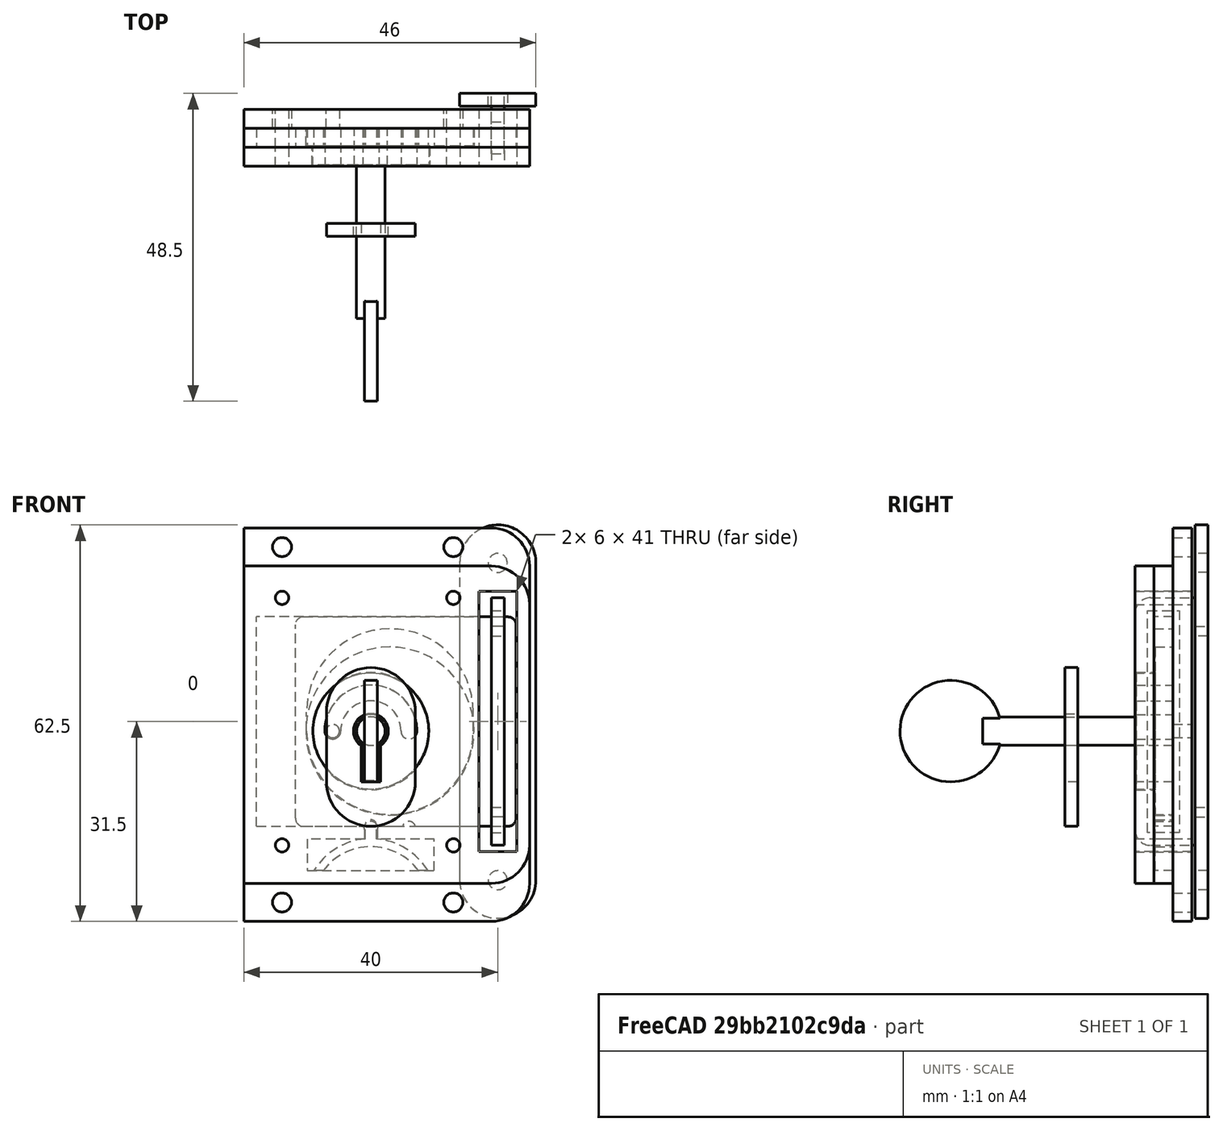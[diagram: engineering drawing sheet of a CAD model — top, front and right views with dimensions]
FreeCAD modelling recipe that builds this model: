
FCSTD DOCUMENT  (FreeCAD 0.21R33492 (Git))
Label: DoorLock
License: All rights reserved
LicenseURL: http://en.wikipedia.org/wiki/All_rights_reserved
objects: TechDraw::DrawViewDimension×39, Sketcher::SketchObject×13, Part::Extrusion×10, TechDraw::DrawViewPart×6, TechDraw::DrawHatch×3, Part::MultiFuse×2, TechDraw::DrawSVGTemplate×2, App::DocumentObjectGroup×2, Part::Cylinder×2, TechDraw::DrawPage×2, Part::Box×1
note: 28 computed .brp shape members not serialized (recipe doc carries the construction recipe); baked Part::Feature solids carry a one-line shape summary decoded from their .brp

FEATURE [Sketcher::SketchObject] Sketch  label="TopPartShape"
  FullyConstrained = true
  Placement = pos=(0,0,0) rot=(1,0,0;1.5708rad)
  sketch-geometry (9):
    g0: ArcOfCircle CenterX=0 CenterY=0 CenterZ=0 NormalX=0 NormalY=0 NormalZ=1 AngleXU=0 Radius=2.625 StartAngle=5.20871 EndAngle=10.4993
    g1: LineSegment StartX=-1.25 StartY=-2.30827 StartZ=0 EndX=-1.25 EndY=-8 EndZ=0
    g2: LineSegment StartX=-1.25 StartY=-8 StartZ=0 EndX=1.25 EndY=-8 EndZ=0
    g3: LineSegment StartX=1.25 StartY=-8 StartZ=0 EndX=1.25 EndY=-2.30827 EndZ=0
    g4: Circle CenterX=0 CenterY=0 CenterZ=0 NormalX=0 NormalY=0 NormalZ=1 AngleXU=0 Radius=9.25
    g5: ArcOfCircle CenterX=-6 CenterY=0 CenterZ=0 NormalX=0 NormalY=0 NormalZ=1 AngleXU=0 Radius=1.25 StartAngle=3.14159 EndAngle=6.28319
    g6: ArcOfCircle CenterX=6 CenterY=0 CenterZ=0 NormalX=0 NormalY=0 NormalZ=1 AngleXU=0 Radius=1.25 StartAngle=3.14159 EndAngle=6.28319
    g7: ArcOfCircle CenterX=0 CenterY=0 CenterZ=0 NormalX=0 NormalY=0 NormalZ=1 AngleXU=0 Radius=7.25 StartAngle=0 EndAngle=3.14159
    g8: ArcOfCircle CenterX=0 CenterY=0 CenterZ=0 NormalX=0 NormalY=0 NormalZ=1 AngleXU=0 Radius=4.75 StartAngle=0 EndAngle=3.14159
  constraints (28):
    c: Coincident(g0,g-1)
    c: Coincident(g1,g0)
    c: Vertical(g1)
    c: Coincident(g2,g1)
    c: Horizontal(g2)
    c: Coincident(g3,g2)
    c: Coincident(g3,g0)
    c: Vertical(g3)
    c: Diameter(g0) = 5.25
    c: Distance(g2) = 2.5
    c: Horizontal(g0,g0)
    c: DistanceY(g2,g0) = 8
    c: Coincident(g4,g0)
    c: Diameter(g4) = 18.5
    c: PointOnObject(g5,g-1)
    c: PointOnObject(g5,g-1)
    c: PointOnObject(g5,g-1)
    c: PointOnObject(g6,g-1)
    c: PointOnObject(g6,g-1)
    c: PointOnObject(g6,g-1)
    c: Coincident(g7,g0)
    c: Coincident(g7,g5)
    c: Coincident(g7,g6)
    c: Coincident(g8,g0)
    c: Coincident(g8,g5)
    c: Coincident(g8,g6)
    c: Diameter(g5) = 2.5
    c: DistanceX(g5,g6) = 12
FEATURE [Sketcher::SketchObject] Sketch001  label="BottomPartShape"
  FullyConstrained = true
  Placement = pos=(0,0,0) rot=(1,0,0;1.5708rad)
  expr: Constraints[20] = Sketch.Constraints[8]
  expr: Constraints[21] = Sketch.Constraints[9]
  expr: Constraints[23] = Sketch.Constraints[11]
  expr: Constraints[36] = Sketch.Constraints[26]
  expr: Constraints[37] = Sketch.Constraints[27]
  sketch-geometry (13):
    g0: Circle CenterX=0 CenterY=0 CenterZ=0 NormalX=0 NormalY=0 NormalZ=1 AngleXU=0 Radius=10.25
    g1: GeomPoint X=-10.25 Y=0 Z=0
    g2: Circle CenterX=3 CenterY=0 CenterZ=0 NormalX=0 NormalY=0 NormalZ=1 AngleXU=0 Radius=13.25
    g3: GeomPoint X=16.25 Y=0 Z=0
    g4: GeomPoint X=10.25 Y=0 Z=0
    g5: ArcOfCircle CenterX=0 CenterY=0 CenterZ=0 NormalX=0 NormalY=0 NormalZ=1 AngleXU=0 Radius=2.625 StartAngle=5.20871 EndAngle=10.4993
    g6: LineSegment StartX=-1.25 StartY=-2.30827 StartZ=0 EndX=-1.25 EndY=-8 EndZ=0
    g7: LineSegment StartX=-1.25 StartY=-8 StartZ=0 EndX=1.25 EndY=-8 EndZ=0
    g8: LineSegment StartX=1.25 StartY=-8 StartZ=0 EndX=1.25 EndY=-2.30827 EndZ=0
    g9: ArcOfCircle CenterX=-6 CenterY=0 CenterZ=0 NormalX=0 NormalY=0 NormalZ=1 AngleXU=0 Radius=1.25 StartAngle=3.14159 EndAngle=6.28319
    g10: ArcOfCircle CenterX=6 CenterY=0 CenterZ=0 NormalX=0 NormalY=0 NormalZ=1 AngleXU=0 Radius=1.25 StartAngle=3.14159 EndAngle=6.28319
    g11: ArcOfCircle CenterX=0 CenterY=0 CenterZ=0 NormalX=0 NormalY=0 NormalZ=1 AngleXU=0 Radius=7.25 StartAngle=0 EndAngle=3.14159
    g12: ArcOfCircle CenterX=0 CenterY=0 CenterZ=0 NormalX=0 NormalY=0 NormalZ=1 AngleXU=0 Radius=4.75 StartAngle=0 EndAngle=3.14159
  constraints (38):
    c: Diameter(g0) = 20.5
    c: PointOnObject(g1,g-1)
    c: PointOnObject(g1,g0)
    c: PointOnObject(g2,g-1)
    c: PointOnObject(g1,g2)
    c: Diameter(g2) = 26.5
    c: PointOnObject(g3,g-1)
    c: PointOnObject(g3,g2)
    c: PointOnObject(g4,g0)
    c: PointOnObject(g4,g-1)
    c: DistanceX(g4,g3) = 6
    c: Coincident(g0,g-1)
    c: Coincident(g5,g-1)
    c: Coincident(g6,g5)
    c: Vertical(g6)
    c: Coincident(g7,g6)
    c: Horizontal(g7)
    c: Coincident(g8,g7)
    c: Coincident(g8,g5)
    c: Vertical(g8)
    c: Diameter(g5) = 5.25
    c: Distance(g7) = 2.5
    c: Horizontal(g5,g5)
    c: DistanceY(g7,g5) = 8
    c: PointOnObject(g9,g-1)
    c: PointOnObject(g9,g-1)
    c: PointOnObject(g9,g-1)
    c: PointOnObject(g10,g-1)
    c: PointOnObject(g10,g-1)
    c: PointOnObject(g10,g-1)
    c: Coincident(g11,g5)
    c: Coincident(g11,g9)
    c: Coincident(g11,g10)
    c: Coincident(g12,g5)
    c: Coincident(g12,g9)
    c: Coincident(g12,g10)
    c: Diameter(g9) = 2.5
    c: DistanceX(g9,g10) = 12
FEATURE [Sketcher::SketchObject] Sketch002  label="SliderShape"
  FullyConstrained = true
  Placement = pos=(0,0,0) rot=(1,0,0;1.5708rad)
  sketch-geometry (25):
    g0: LineSegment StartX=-10.625 StartY=18 StartZ=0 EndX=21.625 EndY=18 EndZ=0
    g1: LineSegment StartX=21.625 StartY=-15 StartZ=0 EndX=-10.625 EndY=-15 EndZ=0
    g2: LineSegment StartX=-11.875 StartY=-13.75 StartZ=0 EndX=-11.875 EndY=16.75 EndZ=0
    g3: LineSegment StartX=22.875 StartY=16.75 StartZ=0 EndX=22.875 EndY=-13.75 EndZ=0
    g4: ArcOfCircle CenterX=3 CenterY=3 CenterZ=0 NormalX=0 NormalY=0 NormalZ=1 AngleXU=0 Radius=13.125 StartAngle=0 EndAngle=3.14159
    g5: ArcOfCircle CenterX=3 CenterY=0 CenterZ=0 NormalX=0 NormalY=0 NormalZ=1 AngleXU=0 Radius=13.125 StartAngle=3.14159 EndAngle=6.28319
    g6: LineSegment StartX=-10.125 StartY=1.6e-15 StartZ=0 EndX=-10.125 EndY=3 EndZ=0
    g7: LineSegment StartX=16.125 StartY=1.6e-15 StartZ=0 EndX=16.125 EndY=3 EndZ=0
    g8: LineSegment StartX=-10.125 StartY=3 StartZ=0 EndX=16.125 EndY=3 EndZ=0
    g9: LineSegment StartX=16.125 StartY=1.6e-15 StartZ=0 EndX=-10.125 EndY=1.6e-15 EndZ=0
    g10: ArcOfCircle CenterX=-10.625 CenterY=16.75 CenterZ=0 NormalX=0 NormalY=0 NormalZ=1 AngleXU=0 Radius=1.25 StartAngle=1.5708 EndAngle=3.14159
    g11: GeomPoint X=-11.875 Y=18 Z=0
    g12: ArcOfCircle CenterX=-10.625 CenterY=-13.75 CenterZ=0 NormalX=0 NormalY=0 NormalZ=1 AngleXU=0 Radius=1.25 StartAngle=3.14159 EndAngle=4.71239
    g13: GeomPoint X=-11.875 Y=-15 Z=0
    g14: ArcOfCircle CenterX=21.625 CenterY=16.75 CenterZ=0 NormalX=0 NormalY=0 NormalZ=1 AngleXU=0 Radius=1.25 StartAngle=-9e-16 EndAngle=1.5708
    g15: GeomPoint X=22.875 Y=18 Z=0
    g16: ArcOfCircle CenterX=21.625 CenterY=-13.75 CenterZ=0 NormalX=0 NormalY=0 NormalZ=1 AngleXU=0 Radius=1.25 StartAngle=4.71239 EndAngle=6.28319
    g17: GeomPoint X=22.875 Y=-15 Z=0
    g18: LineSegment StartX=-10.625 StartY=-15 StartZ=0 EndX=-1 EndY=-15 EndZ=0
    g19: LineSegment StartX=7 StartY=-15 StartZ=0 EndX=21.625 EndY=-15 EndZ=0
    g20: ArcOfCircle CenterX=-2e-16 CenterY=-15.25 CenterZ=0 NormalX=0 NormalY=0 NormalZ=1 AngleXU=0 Radius=1.03078 StartAngle=0.244979 EndAngle=2.89661
    g21: ArcOfCircle CenterX=6 CenterY=-15.25 CenterZ=0 NormalX=0 NormalY=0 NormalZ=1 AngleXU=0 Radius=1.03078 StartAngle=0.244979 EndAngle=2.89661
    g22: LineSegment StartX=1 StartY=-15 StartZ=0 EndX=3 EndY=-15 EndZ=0
    g23: LineSegment StartX=3 StartY=-15 StartZ=0 EndX=5 EndY=-15 EndZ=0
    g24: LineSegment StartX=-2e-16 StartY=-15.25 StartZ=0 EndX=6 EndY=-15.25 EndZ=0
  constraints (68):
    c: Horizontal(g0)
    c: Horizontal(g1)
    c: Vertical(g2)
    c: Vertical(g3)
    c: Coincident(g6,g5)
    c: Coincident(g6,g4)
    c: Coincident(g7,g5)
    c: Coincident(g7,g4)
    c: Vertical(g6)
    c: Vertical(g7)
    c: DistanceY(g5,g4) = 3
    c: Coincident(g8,g4)
    c: Coincident(g8,g4)
    c: Horizontal(g8)
    c: Coincident(g9,g5)
    c: Coincident(g9,g5)
    c: Horizontal(g9)
    c: PointOnObject(g4,g8)
    c: PointOnObject(g5,g9)
    c: Diameter(g4) = 26.25
    c: PointOnObject(g5,g-1)
    c: DistanceX(g-1,g5) = 3
    c: DistanceX(g11,g-1) = 11.875
    c: Distance(g15,g11) = 34.75
    c: DistanceY(g-1,g11) = 18
    c: PointOnObject(g11,g2)
    c: PointOnObject(g11,g0)
    c: Tangent(g2,g10) = 1.5708
    c: Tangent(g0,g10) = 1.5708
    c: PointOnObject(g13,g2)
    c: PointOnObject(g13,g1)
    c: Tangent(g2,g12) = 1.5708
    c: Tangent(g1,g12) = 1.5708
    c: Equal(g10,g12)
    c: Diameter(g10) = 2.5
    c: PointOnObject(g15,g0)
    c: PointOnObject(g15,g3)
    c: Tangent(g0,g14) = 1.5708
    c: Tangent(g3,g14) = 1.5708
    c: PointOnObject(g17,g1)
    c: PointOnObject(g17,g3)
    c: Tangent(g1,g16) = 1.5708
    c: Tangent(g3,g16) = 1.5708
    c: Equal(g10,g14)
    c: Equal(g10,g16)
    c: Coincident(g18,g12)
    c: PointOnObject(g18,g1)
    c: PointOnObject(g22,g1)
    c: PointOnObject(g23,g1)
    c: PointOnObject(g19,g1)
    c: Coincident(g19,g16)
    c: Coincident(g20,g18)
    c: Coincident(g20,g22)
    c: Coincident(g21,g23)
    c: Coincident(g21,g19)
    c: Equal(g20,g21)
    c: DistanceX(g20,g21) = 6
    c: Coincident(g22,g23)
    c: Equal(g22,g23)
    c: DistanceX(g-1,g22) = 3
    c: PointOnObject(g22,g1)
    c: Coincident(g24,g20)
    c: Coincident(g24,g21)
    c: Horizontal(g24)
    c: DistanceY(g20,g18) = 0.25
    c: DistanceX(g18,g20) = 2
    c: DistanceY(g13,g-1) = 15
    c: DistanceY(g13,g11) = 33
FEATURE [Sketcher::SketchObject] Sketch003  label="SpacerShape"
  FullyConstrained = true
  Placement = pos=(0,0,0) rot=(1,0,0;1.5708rad)
  expr: Constraints[38] = Sketch021.Constraints[8]
  expr: Constraints[39] = Sketch021.Constraints[9]
  expr: Constraints[40] = Sketch021.Constraints[10]
  expr: Constraints[41] = Sketch021.Constraints[11]
  expr: Constraints[70] = Sketch019.Constraints[14]
  expr: Constraints[71] = Sketch019.Constraints[15]
  expr: Constraints[72] = Sketch019.Constraints[16]
  expr: Constraints[73] = Sketch019.Constraints[17]
  expr: Constraints[74] = Sketch019.Constraints[18]
  expr: Constraints[75] = Sketch019.Constraints[19]
  expr: Constraints[76] = Sketch019.Constraints[20]
  expr: Constraints[77] = Sketch019.Constraints[21]
  expr: Constraints[82] = Sketch019.Constraints[26]
  expr: Constraints[94] = Sketch019.Constraints[38]
  sketch-geometry (37):
    g0: LineSegment StartX=17 StartY=18 StartZ=0 EndX=-18 EndY=18 EndZ=0
    g1: LineSegment StartX=-18 StartY=-15 StartZ=0 EndX=-18 EndY=18 EndZ=0
    g2: LineSegment StartX=-18 StartY=-15 StartZ=0 EndX=-1.5 EndY=-15 EndZ=0
    g3: LineSegment StartX=1.5 StartY=-15 StartZ=0 EndX=17 EndY=-15 EndZ=0
    g4: LineSegment StartX=-1 StartY=-15.5 StartZ=0 EndX=-1 EndY=-17 EndZ=0
    g5: LineSegment StartX=1 StartY=-15.5 StartZ=0 EndX=1 EndY=-17 EndZ=0
    g6: LineSegment StartX=-1 StartY=-17 StartZ=0 EndX=-10 EndY=-17 EndZ=0
    g7: LineSegment StartX=-10 StartY=-17 StartZ=0 EndX=-10 EndY=-22 EndZ=0
    g8: LineSegment StartX=-10 StartY=-22 StartZ=0 EndX=10 EndY=-22 EndZ=0
    g9: LineSegment StartX=10 StartY=-22 StartZ=0 EndX=10 EndY=-17 EndZ=0
    g10: LineSegment StartX=10 StartY=-17 StartZ=0 EndX=1 EndY=-17 EndZ=0
    g11: GeomPoint X=0 Y=0 Z=0
    g12: ArcOfCircle CenterX=-1.5 CenterY=-15.5 CenterZ=0 NormalX=0 NormalY=0 NormalZ=1 AngleXU=0 Radius=0.5 StartAngle=-9e-16 EndAngle=1.5708
    g13: GeomPoint X=-1 Y=-15 Z=0
    g14: ArcOfCircle CenterX=1.5 CenterY=-15.5 CenterZ=0 NormalX=0 NormalY=0 NormalZ=1 AngleXU=0 Radius=0.5 StartAngle=1.5708 EndAngle=3.14159
    g15: GeomPoint X=1 Y=-15 Z=0
    g16: LineSegment StartX=17 StartY=22 StartZ=0 EndX=23 EndY=22 EndZ=0
    g17: LineSegment StartX=23 StartY=22 StartZ=0 EndX=23 EndY=-19 EndZ=0
    g18: LineSegment StartX=23 StartY=-19 StartZ=0 EndX=17 EndY=-19 EndZ=0
    g19: LineSegment StartX=17 StartY=18 StartZ=0 EndX=17 EndY=22 EndZ=0
    g20: LineSegment StartX=17 StartY=-15 StartZ=0 EndX=17 EndY=-19 EndZ=0
    g21: LineSegment StartX=-14 StartY=21 StartZ=0 EndX=13 EndY=21 EndZ=0
    g22: LineSegment StartX=13 StartY=21 StartZ=0 EndX=13 EndY=-18 EndZ=0
    g23: LineSegment StartX=13 StartY=-18 StartZ=0 EndX=-14 EndY=-18 EndZ=0
    g24: LineSegment StartX=-14 StartY=-18 StartZ=0 EndX=-14 EndY=21 EndZ=0
    g25: LineSegment StartX=-20 StartY=26 StartZ=0 EndX=19 EndY=26 EndZ=0
    g26: LineSegment StartX=25 StartY=20 StartZ=0 EndX=25 EndY=-18 EndZ=0
    g27: LineSegment StartX=19 StartY=-24 StartZ=0 EndX=-20 EndY=-24 EndZ=0
    g28: LineSegment StartX=-20 StartY=-24 StartZ=0 EndX=-20 EndY=26 EndZ=0
    g29: Circle CenterX=-14 CenterY=21 CenterZ=0 NormalX=0 NormalY=0 NormalZ=1 AngleXU=0 Radius=1.05
    g30: Circle CenterX=13 CenterY=21 CenterZ=0 NormalX=0 NormalY=0 NormalZ=1 AngleXU=0 Radius=1.05
    g31: Circle CenterX=-14 CenterY=-18 CenterZ=0 NormalX=0 NormalY=0 NormalZ=1 AngleXU=0 Radius=1.05
    g32: Circle CenterX=13 CenterY=-18 CenterZ=0 NormalX=0 NormalY=0 NormalZ=1 AngleXU=0 Radius=1.05
    g33: ArcOfCircle CenterX=19 CenterY=20 CenterZ=0 NormalX=0 NormalY=0 NormalZ=1 AngleXU=0 Radius=6 StartAngle=1e-16 EndAngle=1.5708
    g34: GeomPoint X=25 Y=26 Z=0
    g35: ArcOfCircle CenterX=19 CenterY=-18 CenterZ=0 NormalX=0 NormalY=0 NormalZ=1 AngleXU=0 Radius=6 StartAngle=4.71239 EndAngle=6.28319
    g36: GeomPoint X=25 Y=-24 Z=0
  constraints (96):
    c: Horizontal(g0)
    c: DistanceX(g0,g-1) = 18
    c: Coincident(g1,g0)
    c: Vertical(g1)
    c: Coincident(g2,g1)
    c: Vertical(g4)
    c: Symmetric(g13,g15,g-2)
    c: Horizontal(g2)
    c: Horizontal(g3)
    c: DistanceX(g13,g15) = 2
    c: Horizontal(g6)
    c: Coincident(g7,g6)
    c: Vertical(g7)
    c: Coincident(g8,g7)
    c: Horizontal(g8)
    c: Coincident(g9,g8)
    c: Vertical(g9)
    c: Coincident(g10,g9)
    c: Horizontal(g10)
    c: Distance(g8) = 20
    c: Distance(g9) = 5
    c: Coincident(g11,g-1)
    c: PointOnObject(g13,g4)
    c: PointOnObject(g13,g2)
    c: Tangent(g4,g12) = 1.5708
    c: Tangent(g2,g12) = 1.5708
    c: PointOnObject(g15,g5)
    c: PointOnObject(g15,g3)
    c: Tangent(g5,g14) = -1.5708
    c: Tangent(g3,g14) = 1.5708
    c: Diameter(g12) = 1
    c: Equal(g12,g14)
    c: Equal(g6,g10)
    c: Coincident(g16,g17)
    c: Coincident(g17,g18)
    c: Horizontal(g16)
    c: Horizontal(g18)
    c: Vertical(g17)
    c: DistanceY(g-1,g16) = 22
    c: DistanceY(g18,g-1) = 19
    c: Distance(g16) = 6
    c: DistanceX(g-1,g16) = 17
    c: DistanceY(g11,g0) = 18
    c: DistanceY(g1,g11) = 15
    c: Coincident(g19,g0)
    c: Coincident(g19,g16)
    c: Vertical(g19)
    c: Coincident(g20,g3)
    c: Coincident(g20,g18)
    c: Vertical(g20)
    c: Vertical(g0,g3)
    c: Coincident(g4,g6)
    c: Coincident(g5,g10)
    c: Vertical(g5)
    c: Horizontal(g4,g5)
    c: DistanceY(g5,g15) = 2
    c: Coincident(g21,g22)
    c: Coincident(g22,g23)
    c: Coincident(g23,g24)
    c: Coincident(g24,g21)
    c: Horizontal(g21)
    c: Horizontal(g23)
    c: Vertical(g22)
    c: Vertical(g24)
    c: Coincident(g27,g28)
    c: Coincident(g28,g25)
    c: Horizontal(g25)
    c: Horizontal(g27)
    c: Vertical(g26)
    c: Vertical(g28)
    c: DistanceX(g27,g-1) = 20
    c: DistanceX(g-1,g36) = 25
    c: DistanceY(g36,g-1) = 24
    c: DistanceY(g-1,g34) = 26
    c: DistanceY(g21,g34) = 5
    c: DistanceY(g36,g22) = 6
    c: DistanceX(g21,g34) = 12
    c: DistanceX(g25,g21) = 6
    c: Coincident(g29,g21)
    c: Coincident(g30,g21)
    c: Coincident(g31,g23)
    c: Coincident(g32,g22)
    c: Diameter(g31) = 2.1
    c: Equal(g31,g29)
    c: Equal(g30,g31)
    c: Equal(g31,g32)
    c: PointOnObject(g34,g25)
    c: PointOnObject(g34,g26)
    c: Tangent(g25,g33) = 1.5708
    c: Tangent(g26,g33) = 1.5708
    c: PointOnObject(g36,g27)
    c: PointOnObject(g36,g26)
    c: Tangent(g27,g35) = 1.5708
    c: Tangent(g26,g35) = 1.5708
    c: Diameter(g33) = 12
    c: Equal(g33,g35)
FEATURE [Sketcher::SketchObject] Sketch004  label="DoorAndWall"
  FullyConstrained = true
  Placement = pos=(0,0,0) rot=(1,0,0;1.5708rad)
  sketch-geometry (14):
    g0: LineSegment StartX=10 StartY=50 StartZ=0 EndX=30 EndY=50 EndZ=0
    g1: LineSegment StartX=30 StartY=50 StartZ=0 EndX=30 EndY=-50 EndZ=0
    g2: LineSegment StartX=30 StartY=-50 StartZ=0 EndX=10 EndY=-50 EndZ=0
    g3: LineSegment StartX=10 StartY=-50 StartZ=0 EndX=10 EndY=50 EndZ=0
    g4: LineSegment StartX=17 StartY=50 StartZ=0 EndX=17 EndY=-50 EndZ=0
    g5: LineSegment StartX=23 StartY=-50 StartZ=0 EndX=23 EndY=50 EndZ=0
    g6: LineSegment StartX=19 StartY=50 StartZ=0 EndX=19 EndY=-50 EndZ=0
    g7: LineSegment StartX=21 StartY=-50 StartZ=0 EndX=21 EndY=50 EndZ=0
    g8: LineSegment StartX=-30 StartY=75 StartZ=0 EndX=-30 EndY=-75 EndZ=0
    g9: LineSegment StartX=-30 StartY=-75 StartZ=0 EndX=30 EndY=-75 EndZ=0
    g10: LineSegment StartX=30 StartY=-75 StartZ=0 EndX=30 EndY=75 EndZ=0
    g11: LineSegment StartX=30 StartY=75 StartZ=0 EndX=-30 EndY=75 EndZ=0
    g12: GeomPoint X=0 Y=0 Z=0
    g13: LineSegment StartX=-20 StartY=-75 StartZ=0 EndX=-20 EndY=75 EndZ=0
  constraints (46):
    c: Coincident(g0,g1)
    c: Coincident(g1,g2)
    c: Coincident(g2,g3)
    c: Coincident(g3,g0)
    c: Horizontal(g0)
    c: Horizontal(g2)
    c: Vertical(g3)
    c: Symmetric(g0,g1,g-1)
    c: Distance(g2) = 20
    c: Distance(g1) = 100
    c: PointOnObject(g4,g0)
    c: PointOnObject(g4,g2)
    c: Vertical(g4)
    c: PointOnObject(g5,g2)
    c: PointOnObject(g5,g0)
    c: Vertical(g5)
    c: DistanceX(g0,g4) = 7
    c: DistanceX(g5,g0) = 7
    c: DistanceX(g4,g5) = 6
    c: PointOnObject(g6,g0)
    c: PointOnObject(g6,g2)
    c: Vertical(g6)
    c: PointOnObject(g7,g2)
    c: PointOnObject(g7,g0)
    c: Vertical(g7)
    c: DistanceX(g6,g7) = 2
    c: DistanceX(g4,g6) = 2
    c: DistanceX(g7,g5) = 2
    c: DistanceX(g-1,g2) = 10
    c: Coincident(g8,g9)
    c: Coincident(g9,g10)
    c: Coincident(g10,g11)
    c: Coincident(g11,g8)
    c: Horizontal(g9)
    c: Horizontal(g11)
    c: Vertical(g10)
    c: Coincident(g12,g-1)
    c: Distance(g8) = 150
    c: PointOnObject(g13,g9)
    c: PointOnObject(g13,g11)
    c: Vertical(g13)
    c: DistanceX(g8,g13) = 10
    c: Distance(g9) = 60
    c: DistanceX(g12,g10) = 30
    c: DistanceX(g8,g12) = 30
    c: Symmetric(g8,g8,g-1)
FEATURE [Part::Extrusion] Extrude  label="BottomPart"
  Base = -> Sketch001
  Dir = (0,-1,2e-16)
  DirMode = 2
  FaceMakerClass = Part::FaceMakerBullseye
  LengthFwd = 2.8
  LengthRev = 0
  Solid = true
  Symmetric = false
FEATURE [Sketcher::SketchObject] Sketch018  label="SpringShape"
  FullyConstrained = true
  Placement = pos=(0,0,0) rot=(1,0,0;1.5708rad)
  sketch-geometry (13):
    g0: LineSegment StartX=-0.9 StartY=-5 StartZ=0 EndX=-0.9 EndY=-7.125 EndZ=0
    g1: LineSegment StartX=0.9 StartY=-5 StartZ=0 EndX=0.9 EndY=-7.125 EndZ=0
    g2: ArcOfCircle CenterX=-6.784e-13 CenterY=-7.125 CenterZ=0 NormalX=0 NormalY=0 NormalZ=1 AngleXU=0 Radius=0.9 StartAngle=3.14159 EndAngle=6.28319
    g3: LineSegment StartX=-0.9 StartY=-7.125 StartZ=0 EndX=0.9 EndY=-7.125 EndZ=0
    g4: ArcOfCircle CenterX=0 CenterY=5.519 CenterZ=0 NormalX=0 NormalY=0 NormalZ=1 AngleXU=0 Radius=10.5574 StartAngle=3.69168 EndAngle=4.62704
    g5: ArcOfCircle CenterX=0 CenterY=5.519 CenterZ=0 NormalX=0 NormalY=0 NormalZ=1 AngleXU=0 Radius=10.5574 StartAngle=4.79774 EndAngle=5.7331
    g6: ArcOfCircle CenterX=0 CenterY=5.519 CenterZ=0 NormalX=0 NormalY=0 NormalZ=1 AngleXU=0 Radius=9.31179 StartAngle=3.77599 EndAngle=5.64879
    g7: LineSegment StartX=-9 StartY=1.8e-15 StartZ=0 EndX=-7.5 EndY=1.8e-15 EndZ=0
    g8: LineSegment StartX=7.5 StartY=1.8e-15 StartZ=0 EndX=9 EndY=1.8e-15 EndZ=0
    g9: LineSegment StartX=-9 StartY=1.8e-15 StartZ=0 EndX=-9 EndY=-5 EndZ=0
    g10: LineSegment StartX=-9 StartY=-5 StartZ=0 EndX=-0.9 EndY=-5 EndZ=0
    g11: LineSegment StartX=0.9 StartY=-5 StartZ=0 EndX=9 EndY=-5 EndZ=0
    g12: LineSegment StartX=9 StartY=-5 StartZ=0 EndX=9 EndY=1.8e-15 EndZ=0
  constraints (38):
    c: DistanceX(g4,g5) = 18
    c: Horizontal(g4,g5)
    c: Vertical(g0)
    c: Vertical(g1)
    c: Coincident(g2,g0)
    c: Coincident(g2,g1)
    c: Horizontal(g0,g1)
    c: Coincident(g3,g0)
    c: Coincident(g3,g1)
    c: Horizontal(g3)
    c: PointOnObject(g2,g3)
    c: Distance(g3) = 1.8
    c: Coincident(g4,g0)
    c: Coincident(g5,g1)
    c: Coincident(g6,g5)
    c: Coincident(g7,g4)
    c: Coincident(g7,g6)
    c: Horizontal(g7)
    c: Coincident(g8,g6)
    c: Coincident(g8,g5)
    c: Horizontal(g8)
    c: Distance(g8) = 1.5
    c: Coincident(g9,g4)
    c: Coincident(g10,g9)
    c: Coincident(g10,g0)
    c: Horizontal(g10)
    c: Coincident(g11,g1)
    c: Horizontal(g11)
    c: Coincident(g12,g11)
    c: Coincident(g12,g5)
    c: Vertical(g12)
    c: Vertical(g9)
    c: Equal(g10,g11)
    c: Distance(g12) = 5
    c: Distance(g1) = 2.125
    c: Coincident(g5,g4)
    c: PointOnObject(g4,g-2)
    c: PointOnObject(g6,g-1)
FEATURE [Part::Extrusion] Extrude012  label="Slider"
  Base = -> Sketch002
  Dir = (0,-1,2e-16)
  DirMode = 2
  FaceMakerClass = Part::FaceMakerBullseye
  LengthFwd = 3
  LengthRev = 0
  Solid = true
  Symmetric = false
FEATURE [Part::Extrusion] Extrude013  label="TopPart"
  Base = -> Sketch
  Dir = (0,-1,2e-16)
  DirMode = 2
  FaceMakerClass = Part::FaceMakerBullseye
  LengthFwd = 3
  LengthRev = 0
  Placement = pos=(0,-2.8,0) rot=(0,0,1;0rad)
  Solid = true
  Symmetric = false
FEATURE [Part::Extrusion] Extrude014  label="Spring"
  Base = -> Sketch018
  Dir = (0,-1,2e-16)
  DirMode = 2
  FaceMakerClass = Part::FaceMakerBullseye
  LengthFwd = 2.8
  LengthRev = 0
  Placement = pos=(0,0,-22) rot=(0,1,0;3.14159rad)
  Solid = true
  Symmetric = false
FEATURE [Sketcher::SketchObject] Sketch019  label="BlankPlateShape"
  FullyConstrained = true
  Placement = pos=(0,0,0) rot=(1,0,0;1.5708rad)
  sketch-geometry (16):
    g0: LineSegment StartX=-14 StartY=21 StartZ=0 EndX=13 EndY=21 EndZ=0
    g1: LineSegment StartX=13 StartY=21 StartZ=0 EndX=13 EndY=-18 EndZ=0
    g2: LineSegment StartX=13 StartY=-18 StartZ=0 EndX=-14 EndY=-18 EndZ=0
    g3: LineSegment StartX=-14 StartY=-18 StartZ=0 EndX=-14 EndY=21 EndZ=0
    g4: LineSegment StartX=-20 StartY=26 StartZ=0 EndX=19 EndY=26 EndZ=0
    g5: LineSegment StartX=25 StartY=20 StartZ=0 EndX=25 EndY=-18 EndZ=0
    g6: LineSegment StartX=19 StartY=-24 StartZ=0 EndX=-20 EndY=-24 EndZ=0
    g7: LineSegment StartX=-20 StartY=-24 StartZ=0 EndX=-20 EndY=26 EndZ=0
    g8: Circle CenterX=-14 CenterY=21 CenterZ=0 NormalX=0 NormalY=0 NormalZ=1 AngleXU=0 Radius=1.05
    g9: Circle CenterX=13 CenterY=21 CenterZ=0 NormalX=0 NormalY=0 NormalZ=1 AngleXU=0 Radius=1.05
    g10: Circle CenterX=-14 CenterY=-18 CenterZ=0 NormalX=0 NormalY=0 NormalZ=1 AngleXU=0 Radius=1.05
    g11: Circle CenterX=13 CenterY=-18 CenterZ=0 NormalX=0 NormalY=0 NormalZ=1 AngleXU=0 Radius=1.05
    g12: ArcOfCircle CenterX=19 CenterY=20 CenterZ=0 NormalX=0 NormalY=0 NormalZ=1 AngleXU=0 Radius=6 StartAngle=1e-16 EndAngle=1.5708
    g13: GeomPoint X=25 Y=26 Z=0
    g14: ArcOfCircle CenterX=19 CenterY=-18 CenterZ=0 NormalX=0 NormalY=0 NormalZ=1 AngleXU=0 Radius=6 StartAngle=4.71239 EndAngle=6.28319
    g15: GeomPoint X=25 Y=-24 Z=0
  constraints (40):
    c: Coincident(g0,g1)
    c: Coincident(g1,g2)
    c: Coincident(g2,g3)
    c: Coincident(g3,g0)
    c: Horizontal(g0)
    c: Horizontal(g2)
    c: Vertical(g1)
    c: Vertical(g3)
    c: Coincident(g6,g7)
    c: Coincident(g7,g4)
    c: Horizontal(g4)
    c: Horizontal(g6)
    c: Vertical(g5)
    c: Vertical(g7)
    c: DistanceX(g6,g-1) = 20
    c: DistanceX(g-1,g15) = 25
    c: DistanceY(g15,g-1) = 24
    c: DistanceY(g-1,g13) = 26
    c: DistanceY(g0,g13) = 5
    c: DistanceY(g15,g1) = 6
    c: DistanceX(g0,g13) = 12
    c: DistanceX(g4,g0) = 6
    c: Coincident(g8,g0)
    c: Coincident(g9,g0)
    c: Coincident(g10,g2)
    c: Coincident(g11,g1)
    c: Diameter(g10) = 2.1
    c: Equal(g10,g8)
    c: Equal(g9,g10)
    c: Equal(g10,g11)
    c: PointOnObject(g13,g4)
    c: PointOnObject(g13,g5)
    c: Tangent(g4,g12) = 1.5708
    c: Tangent(g5,g12) = 1.5708
    c: PointOnObject(g15,g6)
    c: PointOnObject(g15,g5)
    c: Tangent(g6,g14) = 1.5708
    c: Tangent(g5,g14) = 1.5708
    c: Diameter(g12) = 12
    c: Equal(g12,g14)
FEATURE [Sketcher::SketchObject] Sketch020  label="FrontPlateShape"
  FullyConstrained = true
  Placement = pos=(0,0,0) rot=(1,0,0;1.5708rad)
  expr: Constraints[16] = Sketch019.Constraints[14]
  expr: Constraints[17] = Sketch019.Constraints[15]
  expr: Constraints[18] = Sketch019.Constraints[16]
  expr: Constraints[19] = Sketch019.Constraints[17]
  expr: Constraints[20] = Sketch019.Constraints[18]
  expr: Constraints[21] = Sketch019.Constraints[19]
  expr: Constraints[22] = Sketch019.Constraints[20]
  expr: Constraints[23] = Sketch019.Constraints[21]
  expr: Constraints[28] = Sketch019.Constraints[26]
  expr: Constraints[40] = Sketch019.Constraints[38]
  sketch-geometry (21):
    g0: Circle CenterX=0 CenterY=0 CenterZ=0 NormalX=0 NormalY=0 NormalZ=1 AngleXU=0 Radius=9.125
    g1: LineSegment StartX=-14 StartY=21 StartZ=0 EndX=13 EndY=21 EndZ=0
    g2: LineSegment StartX=13 StartY=21 StartZ=0 EndX=13 EndY=-18 EndZ=0
    g3: LineSegment StartX=13 StartY=-18 StartZ=0 EndX=-14 EndY=-18 EndZ=0
    g4: LineSegment StartX=-14 StartY=-18 StartZ=0 EndX=-14 EndY=21 EndZ=0
    g5: LineSegment StartX=-20 StartY=26 StartZ=0 EndX=19 EndY=26 EndZ=0
    g6: LineSegment StartX=25 StartY=20 StartZ=0 EndX=25 EndY=-18 EndZ=0
    g7: LineSegment StartX=19 StartY=-24 StartZ=0 EndX=-20 EndY=-24 EndZ=0
    g8: LineSegment StartX=-20 StartY=-24 StartZ=0 EndX=-20 EndY=26 EndZ=0
    g9: Circle CenterX=-14 CenterY=21 CenterZ=0 NormalX=0 NormalY=0 NormalZ=1 AngleXU=0 Radius=1.05
    g10: Circle CenterX=13 CenterY=21 CenterZ=0 NormalX=0 NormalY=0 NormalZ=1 AngleXU=0 Radius=1.05
    g11: Circle CenterX=-14 CenterY=-18 CenterZ=0 NormalX=0 NormalY=0 NormalZ=1 AngleXU=0 Radius=1.05
    g12: Circle CenterX=13 CenterY=-18 CenterZ=0 NormalX=0 NormalY=0 NormalZ=1 AngleXU=0 Radius=1.05
    g13: ArcOfCircle CenterX=19 CenterY=20 CenterZ=0 NormalX=0 NormalY=0 NormalZ=1 AngleXU=0 Radius=6 StartAngle=1e-16 EndAngle=1.5708
    g14: GeomPoint X=25 Y=26 Z=0
    g15: ArcOfCircle CenterX=19 CenterY=-18 CenterZ=0 NormalX=0 NormalY=0 NormalZ=1 AngleXU=0 Radius=6 StartAngle=4.71239 EndAngle=6.28319
    g16: GeomPoint X=25 Y=-24 Z=0
    g17: LineSegment StartX=17 StartY=22 StartZ=0 EndX=23 EndY=22 EndZ=0
    g18: LineSegment StartX=23 StartY=22 StartZ=0 EndX=23 EndY=-19 EndZ=0
    g19: LineSegment StartX=23 StartY=-19 StartZ=0 EndX=17 EndY=-19 EndZ=0
    g20: LineSegment StartX=17 StartY=-19 StartZ=0 EndX=17 EndY=22 EndZ=0
  constraints (54):
    c: Coincident(g0,g-1)
    c: Diameter(g0) = 18.25
    c: Coincident(g1,g2)
    c: Coincident(g2,g3)
    c: Coincident(g3,g4)
    c: Coincident(g4,g1)
    c: Horizontal(g1)
    c: Horizontal(g3)
    c: Vertical(g2)
    c: Vertical(g4)
    c: Coincident(g7,g8)
    c: Coincident(g8,g5)
    c: Horizontal(g5)
    c: Horizontal(g7)
    c: Vertical(g6)
    c: Vertical(g8)
    c: DistanceX(g7,g-1) = 20
    c: DistanceX(g-1,g16) = 25
    c: DistanceY(g16,g-1) = 24
    c: DistanceY(g-1,g14) = 26
    c: DistanceY(g1,g14) = 5
    c: DistanceY(g16,g2) = 6
    c: DistanceX(g1,g14) = 12
    c: DistanceX(g5,g1) = 6
    c: Coincident(g9,g1)
    c: Coincident(g10,g1)
    c: Coincident(g11,g3)
    c: Coincident(g12,g2)
    c: Diameter(g11) = 2.1
    c: Equal(g11,g9)
    c: Equal(g10,g11)
    c: Equal(g11,g12)
    c: PointOnObject(g14,g5)
    c: PointOnObject(g14,g6)
    c: Tangent(g5,g13) = 1.5708
    c: Tangent(g6,g13) = 1.5708
    c: PointOnObject(g16,g7)
    c: PointOnObject(g16,g6)
    c: Tangent(g7,g15) = 1.5708
    c: Tangent(g6,g15) = 1.5708
    c: Diameter(g13) = 12
    c: Equal(g13,g15)
    c: Coincident(g17,g18)
    c: Coincident(g18,g19)
    c: Coincident(g19,g20)
    c: Coincident(g20,g17)
    c: Horizontal(g17)
    c: Horizontal(g19)
    c: Vertical(g18)
    c: Vertical(g20)
    c: DistanceY(g19,g0) = 19
    c: DistanceY(g0,g17) = 22
    c: DistanceX(g0,g17) = 17
    c: DistanceX(g0,g17) = 23
FEATURE [Sketcher::SketchObject] Sketch021  label="CutoutShape"
  FullyConstrained = true
  Placement = pos=(0,0,0) rot=(1,0,0;1.5708rad)
  sketch-geometry (4):
    g0: LineSegment StartX=17 StartY=22 StartZ=0 EndX=23 EndY=22 EndZ=0
    g1: LineSegment StartX=23 StartY=22 StartZ=0 EndX=23 EndY=-19 EndZ=0
    g2: LineSegment StartX=23 StartY=-19 StartZ=0 EndX=17 EndY=-19 EndZ=0
    g3: LineSegment StartX=17 StartY=-19 StartZ=0 EndX=17 EndY=22 EndZ=0
  constraints (12):
    c: Coincident(g0,g1)
    c: Coincident(g1,g2)
    c: Coincident(g2,g3)
    c: Coincident(g3,g0)
    c: Horizontal(g0)
    c: Horizontal(g2)
    c: Vertical(g1)
    c: Vertical(g3)
    c: DistanceY(g-1,g0) = 22
    c: DistanceY(g2,g-1) = 19
    c: Distance(g0) = 6
    c: DistanceX(g-1,g0) = 17
FEATURE [Sketcher::SketchObject] Sketch022  label="BackPlateShape"
  FullyConstrained = true
  Placement = pos=(0,0,0) rot=(1,0,0;1.5708rad)
  expr: Constraints[10] = Sketch021.Constraints[10]
  expr: Constraints[11] = Sketch021.Constraints[11]
  expr: Constraints[29] = Sketch019.Constraints[14]
  expr: Constraints[30] = Sketch019.Constraints[15]
  expr: Constraints[35] = Sketch019.Constraints[20]
  expr: Constraints[36] = Sketch019.Constraints[21]
  expr: Constraints[41] = Sketch019.Constraints[26]
  expr: Constraints[53] = Sketch019.Constraints[38]
  expr: Constraints[8] = Sketch021.Constraints[8]
  expr: Constraints[9] = Sketch021.Constraints[9]
  sketch-geometry (31):
    g0: LineSegment StartX=17 StartY=22 StartZ=0 EndX=23 EndY=22 EndZ=0
    g1: LineSegment StartX=23 StartY=22 StartZ=0 EndX=23 EndY=-19 EndZ=0
    g2: LineSegment StartX=23 StartY=-19 StartZ=0 EndX=17 EndY=-19 EndZ=0
    g3: LineSegment StartX=17 StartY=-19 StartZ=0 EndX=17 EndY=22 EndZ=0
    g4: Circle CenterX=-6 CenterY=0 CenterZ=0 NormalX=0 NormalY=0 NormalZ=1 AngleXU=0 Radius=1.05
    g5: LineSegment StartX=-14 StartY=21 StartZ=0 EndX=13 EndY=21 EndZ=0
    g6: LineSegment StartX=13 StartY=21 StartZ=0 EndX=13 EndY=-18 EndZ=0
    g7: LineSegment StartX=13 StartY=-18 StartZ=0 EndX=-14 EndY=-18 EndZ=0
    g8: LineSegment StartX=-14 StartY=-18 StartZ=0 EndX=-14 EndY=21 EndZ=0
    g9: LineSegment StartX=-20 StartY=32 StartZ=0 EndX=19 EndY=32 EndZ=0
    g10: LineSegment StartX=25 StartY=26 StartZ=0 EndX=25 EndY=-24 EndZ=0
    g11: LineSegment StartX=19 StartY=-30 StartZ=0 EndX=-20 EndY=-30 EndZ=0
    g12: LineSegment StartX=-20 StartY=-30 StartZ=0 EndX=-20 EndY=32 EndZ=0
    g13: Circle CenterX=-14 CenterY=21 CenterZ=0 NormalX=0 NormalY=0 NormalZ=1 AngleXU=0 Radius=1.05
    g14: Circle CenterX=13 CenterY=21 CenterZ=0 NormalX=0 NormalY=0 NormalZ=1 AngleXU=0 Radius=1.05
    g15: Circle CenterX=-14 CenterY=-18 CenterZ=0 NormalX=0 NormalY=0 NormalZ=1 AngleXU=0 Radius=1.05
    g16: Circle CenterX=13 CenterY=-18 CenterZ=0 NormalX=0 NormalY=0 NormalZ=1 AngleXU=0 Radius=1.05
    g17: ArcOfCircle CenterX=19 CenterY=26 CenterZ=0 NormalX=0 NormalY=0 NormalZ=1 AngleXU=0 Radius=6 StartAngle=0 EndAngle=1.5708
    g18: GeomPoint X=25 Y=32 Z=0
    g19: ArcOfCircle CenterX=19 CenterY=-24 CenterZ=0 NormalX=0 NormalY=0 NormalZ=1 AngleXU=0 Radius=6 StartAngle=4.71239 EndAngle=6.28319
    g20: GeomPoint X=25 Y=-30 Z=0
    g21: LineSegment StartX=-14 StartY=21 StartZ=0 EndX=-14 EndY=29 EndZ=0
    g22: LineSegment StartX=-14 StartY=29 StartZ=0 EndX=13 EndY=29 EndZ=0
    g23: LineSegment StartX=13 StartY=29 StartZ=0 EndX=13 EndY=21 EndZ=0
    g24: Circle CenterX=-14 CenterY=29 CenterZ=0 NormalX=0 NormalY=0 NormalZ=1 AngleXU=0 Radius=1.5
    g25: Circle CenterX=13 CenterY=29 CenterZ=0 NormalX=0 NormalY=0 NormalZ=1 AngleXU=0 Radius=1.5
    g26: LineSegment StartX=-14 StartY=-18 StartZ=0 EndX=-14 EndY=-27 EndZ=0
    g27: LineSegment StartX=-14 StartY=-27 StartZ=0 EndX=13 EndY=-27 EndZ=0
    g28: LineSegment StartX=13 StartY=-27 StartZ=0 EndX=13 EndY=-18 EndZ=0
    g29: Circle CenterX=-14 CenterY=-27 CenterZ=0 NormalX=0 NormalY=0 NormalZ=1 AngleXU=0 Radius=1.5
    g30: Circle CenterX=13 CenterY=-27 CenterZ=0 NormalX=0 NormalY=0 NormalZ=1 AngleXU=0 Radius=1.5
  constraints (79):
    c: Coincident(g0,g1)
    c: Coincident(g1,g2)
    c: Coincident(g2,g3)
    c: Coincident(g3,g0)
    c: Horizontal(g0)
    c: Horizontal(g2)
    c: Vertical(g1)
    c: Vertical(g3)
    c: DistanceY(g-1,g0) = 22
    c: DistanceY(g2,g-1) = 19
    c: Distance(g0) = 6
    c: DistanceX(g-1,g0) = 17
    c: PointOnObject(g4,g-1)
    c: Diameter(g4) = 2.1
    c: DistanceX(g4,g-1) = 6
    c: Coincident(g5,g6)
    c: Coincident(g6,g7)
    c: Coincident(g7,g8)
    c: Coincident(g8,g5)
    c: Horizontal(g5)
    c: Horizontal(g7)
    c: Vertical(g6)
    c: Vertical(g8)
    c: Coincident(g11,g12)
    c: Coincident(g12,g9)
    c: Horizontal(g9)
    c: Horizontal(g11)
    c: Vertical(g10)
    c: Vertical(g12)
    c: DistanceX(g11,g-1) = 20
    c: DistanceX(g-1,g20) = 25
    c: DistanceY(g20,g-1) = 30
    c: DistanceY(g-1,g18) = 32
    c: DistanceY(g5,g18) = 11
    c: DistanceY(g20,g6) = 12
    c: DistanceX(g5,g18) = 12
    c: DistanceX(g9,g5) = 6
    c: Coincident(g13,g5)
    c: Coincident(g14,g5)
    c: Coincident(g15,g7)
    c: Coincident(g16,g6)
    c: Diameter(g15) = 2.1
    c: Equal(g15,g13)
    c: Equal(g14,g15)
    c: Equal(g15,g16)
    c: PointOnObject(g18,g9)
    c: PointOnObject(g18,g10)
    c: Tangent(g9,g17) = 1.5708
    c: Tangent(g10,g17) = 1.5708
    c: PointOnObject(g20,g11)
    c: PointOnObject(g20,g10)
    c: Tangent(g11,g19) = 1.5708
    c: Tangent(g10,g19) = 1.5708
    c: Diameter(g17) = 12
    c: Equal(g17,g19)
    c: Coincident(g21,g13)
    c: Vertical(g21)
    c: Coincident(g22,g21)
    c: Horizontal(g22)
    c: Coincident(g23,g22)
    c: Coincident(g23,g14)
    c: Vertical(g23)
    c: Distance(g21) = 8
    c: Coincident(g24,g21)
    c: Diameter(g24) = 3
    c: Coincident(g25,g22)
    c: Equal(g24,g25)
    c: Coincident(g26,g15)
    c: Vertical(g26)
    c: Coincident(g27,g26)
    c: Horizontal(g27)
    c: Coincident(g28,g27)
    c: Coincident(g28,g16)
    c: Vertical(g28)
    c: Distance(g26) = 9
    c: Coincident(g29,g26)
    c: Coincident(g30,g27)
    c: Equal(g29,g24)
    c: Equal(g24,g30)
FEATURE [Part::Extrusion] Extrude015  label="Spacer"
  Base = -> Sketch003
  Dir = (0,-1,2e-16)
  DirMode = 2
  FaceMakerClass = Part::FaceMakerBullseye
  LengthFwd = 3
  LengthRev = 0
  Solid = true
  Symmetric = false
FEATURE [Part::Extrusion] Extrude016  label="FrontPlate"
  Base = -> Sketch020
  Dir = (0,-1,2e-16)
  DirMode = 2
  FaceMakerClass = Part::FaceMakerBullseye
  LengthFwd = 3
  LengthRev = 0
  Placement = pos=(0,-3,0) rot=(0,0,1;0rad)
  Solid = true
  Symmetric = false
FEATURE [Part::Extrusion] Extrude017  label="BackPlate"
  Base = -> Sketch022
  Dir = (0,-1,2e-16)
  DirMode = 2
  FaceMakerClass = Part::FaceMakerBullseye
  LengthFwd = 3
  LengthRev = 0
  Placement = pos=(0,3,0) rot=(0,0,1;0rad)
  Solid = true
  Symmetric = false
FEATURE [Part::MultiFuse] Fusion  label="KeyHole"
  Refine = true
  Shapes = -> [Extrude,Extrude013]
FEATURE [Sketcher::SketchObject] Sketch028  label="DoorLockSlotPlateShape"
  FullyConstrained = true
  Placement = pos=(20,0,0) rot=(0.57735,0.57735,0.57735;2.0944rad)
  sketch-geometry (16):
    g0: LineSegment StartX=-4 StartY=19 StartZ=0 EndX=1 EndY=19 EndZ=0
    g1: LineSegment StartX=1 StartY=19 StartZ=0 EndX=1 EndY=-16 EndZ=0
    g2: LineSegment StartX=1 StartY=-16 StartZ=0 EndX=-4 EndY=-16 EndZ=0
    g3: LineSegment StartX=-4 StartY=-16 StartZ=0 EndX=-4 EndY=19 EndZ=0
    g4: LineSegment StartX=-3.5 StartY=21 StartZ=0 EndX=3.5 EndY=21 EndZ=0
    g5: LineSegment StartX=-6 StartY=-15.5 StartZ=0 EndX=-6 EndY=18.5 EndZ=0
    g6: ArcOfCircle CenterX=-3.5 CenterY=18.5 CenterZ=0 NormalX=0 NormalY=0 NormalZ=1 AngleXU=0 Radius=2.5 StartAngle=1.5708 EndAngle=3.14159
    g7: GeomPoint X=-6 Y=21 Z=0
    g8: LineSegment StartX=-3.5 StartY=-18 StartZ=0 EndX=3.5 EndY=-18 EndZ=0
    g9: LineSegment StartX=3.5 StartY=-18 StartZ=0 EndX=3.5 EndY=-12 EndZ=0
    g10: LineSegment StartX=3.5 StartY=-12 StartZ=0 EndX=5.5 EndY=-12 EndZ=0
    g11: LineSegment StartX=5.5 StartY=-12 StartZ=0 EndX=5.5 EndY=15 EndZ=0
    g12: LineSegment StartX=5.5 StartY=15 StartZ=0 EndX=3.5 EndY=15 EndZ=0
    g13: LineSegment StartX=3.5 StartY=15 StartZ=0 EndX=3.5 EndY=21 EndZ=0
    g14: ArcOfCircle CenterX=-3.5 CenterY=-15.5 CenterZ=0 NormalX=0 NormalY=0 NormalZ=1 AngleXU=0 Radius=2.5 StartAngle=3.14159 EndAngle=4.71239
    g15: GeomPoint X=-6 Y=-18 Z=0
  constraints (44):
    c: Coincident(g0,g1)
    c: Coincident(g1,g2)
    c: Coincident(g2,g3)
    c: Coincident(g3,g0)
    c: Horizontal(g0)
    c: Horizontal(g2)
    c: Vertical(g1)
    c: Vertical(g3)
    c: DistanceY(g-1,g0) = 19
    c: DistanceY(g1,g-1) = 16
    c: Horizontal(g4)
    c: Vertical(g5)
    c: DistanceY(g-1,g4) = 21
    c: Distance(g0) = 5
    c: DistanceX(g-1,g0) = 1
    c: PointOnObject(g7,g5)
    c: PointOnObject(g7,g4)
    c: Tangent(g5,g6) = 1.5708
    c: Tangent(g4,g6) = 1.5708
    c: Horizontal(g8)
    c: Coincident(g9,g8)
    c: Vertical(g9)
    c: Coincident(g10,g9)
    c: Horizontal(g10)
    c: Coincident(g11,g10)
    c: Vertical(g11)
    c: Coincident(g12,g11)
    c: Horizontal(g12)
    c: Vertical(g13)
    c: Coincident(g13,g4)
    c: Coincident(g12,g13)
    c: DistanceY(g11,g4) = 6
    c: DistanceY(g8,g10) = 6
    c: DistanceY(g8,g-1) = 18
    c: Equal(g12,g10)
    c: DistanceX(g-1,g8) = 3.5
    c: DistanceX(g8,g10) = 2
    c: PointOnObject(g15,g5)
    c: PointOnObject(g15,g8)
    c: Tangent(g5,g14) = 1.5708
    c: Tangent(g8,g14) = -1.5708
    c: Equal(g14,g6)
    c: Diameter(g14) = 5
    c: DistanceX(g15,g-1) = 6
FEATURE [Part::Extrusion] Extrude022  label="DoorLockSlotPlate"
  Base = -> Sketch028
  Dir = (1,-2e-16,2e-16)
  DirMode = 2
  FaceMakerClass = Part::FaceMakerBullseye
  LengthFwd = 2
  LengthRev = 0
  Solid = true
  Symmetric = true
FEATURE [Sketcher::SketchObject] Sketch029  label="DoorLockMountPlateShape"
  FullyConstrained = true
  Placement = pos=(0,0,0) rot=(0,0.707107,0.707107;3.14159rad)
  sketch-geometry (18):
    g0: LineSegment StartX=1 StartY=16.5 StartZ=0 EndX=1 EndY=-13.5 EndZ=0
    g1: LineSegment StartX=-1 StartY=-13.5 StartZ=0 EndX=-1 EndY=16.5 EndZ=0
    g2: LineSegment StartX=6 StartY=26.5 StartZ=0 EndX=6 EndY=-23.5 EndZ=0
    g3: LineSegment StartX=-6 StartY=-23.5 StartZ=0 EndX=-6 EndY=26.5 EndZ=0
    g4: ArcOfCircle CenterX=0 CenterY=26.5 CenterZ=0 NormalX=0 NormalY=0 NormalZ=1 AngleXU=0 Radius=6 StartAngle=0 EndAngle=3.14159
    g5: ArcOfCircle CenterX=0 CenterY=-23.5 CenterZ=0 NormalX=0 NormalY=0 NormalZ=1 AngleXU=0 Radius=6 StartAngle=3.14159 EndAngle=6.28319
    g6: LineSegment StartX=-6 StartY=-23.5 StartZ=0 EndX=6 EndY=-23.5 EndZ=0
    g7: LineSegment StartX=-6 StartY=26.5 StartZ=0 EndX=6 EndY=26.5 EndZ=0
    g8: LineSegment StartX=-1 StartY=-13.5 StartZ=0 EndX=-6 EndY=-13.5 EndZ=0
    g9: LineSegment StartX=1 StartY=-13.5 StartZ=0 EndX=6 EndY=-13.5 EndZ=0
    g10: LineSegment StartX=0 StartY=-23.5 StartZ=0 EndX=0 EndY=-13.5 EndZ=0
    g11: LineSegment StartX=0 StartY=26.5 StartZ=0 EndX=0 EndY=16.5 EndZ=0
    g12: Circle CenterX=0 CenterY=-23.5 CenterZ=0 NormalX=0 NormalY=0 NormalZ=1 AngleXU=0 Radius=1.5
    g13: Circle CenterX=0 CenterY=26.5 CenterZ=0 NormalX=0 NormalY=0 NormalZ=1 AngleXU=0 Radius=1.5
    g14: LineSegment StartX=-1 StartY=-13.5 StartZ=0 EndX=0 EndY=-13.5 EndZ=0
    g15: LineSegment StartX=0 StartY=-13.5 StartZ=0 EndX=1 EndY=-13.5 EndZ=0
    g16: LineSegment StartX=-1 StartY=16.5 StartZ=0 EndX=0 EndY=16.5 EndZ=0
    g17: LineSegment StartX=0 StartY=16.5 StartZ=0 EndX=1 EndY=16.5 EndZ=0
  constraints (50):
    c: Vertical(g0)
    c: Vertical(g1)
    c: DistanceY(g-1,g0) = 16.5
    c: DistanceY(g0,g-1) = 13.5
    c: Vertical(g2)
    c: Vertical(g3)
    c: Coincident(g4,g3)
    c: Coincident(g4,g2)
    c: Coincident(g5,g3)
    c: Coincident(g5,g2)
    c: Coincident(g6,g3)
    c: Coincident(g6,g2)
    c: Horizontal(g6)
    c: Coincident(g7,g3)
    c: Coincident(g7,g2)
    c: Horizontal(g7)
    c: PointOnObject(g4,g7)
    c: PointOnObject(g5,g6)
    c: DistanceX(g3,g2) = 12
    c: PointOnObject(g8,g3)
    c: Horizontal(g8)
    c: Coincident(g9,g0)
    c: PointOnObject(g9,g2)
    c: Horizontal(g9)
    c: Equal(g8,g9)
    c: Coincident(g10,g5)
    c: Vertical(g10)
    c: Coincident(g11,g4)
    c: Vertical(g11)
    c: Equal(g11,g10)
    c: DistanceY(g3,g3) = 50
    c: Coincident(g12,g5)
    c: Coincident(g13,g4)
    c: Diameter(g13) = 3
    c: Equal(g13,g12)
    c: PointOnObject(g-1,g11)
    c: Coincident(g14,g1)
    c: Coincident(g15,g0)
    c: Coincident(g14,g15)
    c: Horizontal(g14)
    c: Horizontal(g15)
    c: Coincident(g10,g14)
    c: DistanceX(g1,g0) = 2
    c: Coincident(g16,g1)
    c: Coincident(g17,g0)
    c: Coincident(g16,g17)
    c: Horizontal(g16)
    c: Horizontal(g17)
    c: Coincident(g16,g11)
    c: Coincident(g8,g1)
FEATURE [Part::Extrusion] Extrude023  label="DoorLockMountPlate"
  Base = -> Sketch029
  Dir = (0,1,-2e-16)
  DirMode = 2
  FaceMakerClass = Part::FaceMakerBullseye
  LengthFwd = 2
  LengthRev = 0
  Placement = pos=(20,3.5,0) rot=(0,0,1;0rad)
  Solid = true
  Symmetric = false
FEATURE [TechDraw::DrawSVGTemplate] Template
  EditableTexts = AUTHOR_NAME=Lukas Goßmann; DRAWING_TITLE=Schloss und Schließblech; FC-DATE=07.06.2023; FC-REV=REV B; FC-SC=2:1; FC-SH=7/7; FC-SI=A3; FreeCAD_DRAWING=Exzenter / Schlüsselloch und Rastfeder: PLA; SI-1=Schließblech: Messing (vergoldet); SI-2=Schloss Gehäuse und Riegel: Resopal 3mm; SI-4=Zusammenbau mit 5x Federsplint 2mm; SI-5=Montage mit 4x Senkkopfschrauben 3mm
  Height = 297
  Orientation = 1
  Width = 420
FEATURE [TechDraw::DrawViewPart] View
  CoarseView = false
  Direction = (0,-1,0)
  Focus = 100
  HardHidden = false
  IsoCount = 0
  IsoHidden = false
  IsoVisible = false
  LockPosition = false
  Perspective = false
  Rotation = 0
  Scale = 2
  ScaleType = 2
  ScrubCount = 0
  SeamHidden = false
  SeamVisible = true
  SmoothHidden = false
  SmoothVisible = true
  Source = -> [Extrude017,Extrude015,Fusion,Extrude012,Extrude014]
  X = 100
  XDirection = (1,0,0)
  Y = 180
FEATURE [TechDraw::DrawViewPart] View001
  CoarseView = false
  Direction = (1,0,0)
  Focus = 100
  HardHidden = false
  IsoCount = 0
  IsoHidden = false
  IsoVisible = false
  LockPosition = false
  Perspective = false
  Rotation = 0
  Scale = 2
  ScaleType = 2
  ScrubCount = 0
  SeamHidden = false
  SeamVisible = true
  SmoothHidden = false
  SmoothVisible = true
  Source = -> [Extrude023,Extrude022]
  X = 270
  XDirection = (0,-1,0)
  Y = 180
FEATURE [TechDraw::DrawViewPart] View002
  CoarseView = false
  Direction = (0.707,0,0.707)
  Focus = 100
  HardHidden = false
  IsoCount = 0
  IsoHidden = false
  IsoVisible = false
  LockPosition = false
  Perspective = false
  Rotation = 0
  Scale = 2
  ScaleType = 2
  ScrubCount = 0
  SeamHidden = false
  SeamVisible = true
  SmoothHidden = false
  SmoothVisible = true
  Source = -> [Extrude016,Extrude015,Extrude017]
  X = 200
  XDirection = (0,0.707,0)
  Y = 180
FEATURE [TechDraw::DrawViewPart] View003
  CoarseView = false
  Direction = (0,-1,0)
  Focus = 100
  HardHidden = false
  IsoCount = 0
  IsoHidden = false
  IsoVisible = false
  LockPosition = false
  Perspective = false
  Rotation = 0
  Scale = 2
  ScaleType = 2
  ScrubCount = 0
  SeamHidden = false
  SeamVisible = true
  SmoothHidden = false
  SmoothVisible = true
  Source = -> [Extrude023,Extrude022]
  X = 340
  XDirection = (1,0,0)
  Y = 180
FEATURE [TechDraw::DrawViewDimension] Dimension
  AngleOverride = false
  Arbitrary = false
  ArbitraryTolerances = false
  EqualTolerance = true
  ExtensionAngle = 0
  FormatSpec = %.2w
  FormatSpecOverTolerance = %+.2w
  FormatSpecUnderTolerance = %+.2w
  Inverted = false
  LineAngle = 0
  LockPosition = false
  MeasureType = 1
  OverTolerance = 0
  References2D = -> [View003]
  Rotation = 0
  ScaleType = 0
  TheoreticalExact = false
  Type = 2
  UnderTolerance = 0
  X = 34.634
  Y = 2.71975
FEATURE [TechDraw::DrawViewDimension] Dimension001
  AngleOverride = false
  Arbitrary = false
  ArbitraryTolerances = false
  EqualTolerance = true
  ExtensionAngle = 0
  FormatSpec = %.2w
  FormatSpecOverTolerance = %+.2w
  FormatSpecUnderTolerance = %+.2w
  Inverted = false
  LineAngle = 0
  LockPosition = false
  MeasureType = 1
  OverTolerance = 0
  References2D = -> [View003]
  Rotation = 0
  ScaleType = 0
  TheoreticalExact = false
  Type = 2
  UnderTolerance = 0
  X = 24.4142
  Y = 2.06051
FEATURE [TechDraw::DrawViewDimension] Dimension002
  AngleOverride = false
  Arbitrary = false
  ArbitraryTolerances = false
  EqualTolerance = true
  ExtensionAngle = 0
  FormatSpec = %.2w
  FormatSpecOverTolerance = %+.2w
  FormatSpecUnderTolerance = %+.2w
  Inverted = false
  LineAngle = 0
  LockPosition = false
  MeasureType = 1
  OverTolerance = 0
  References2D = -> [View003]
  Rotation = 0
  ScaleType = 0
  TheoreticalExact = false
  Type = 2
  UnderTolerance = 0
  X = 15.4046
  Y = 2.5
FEATURE [TechDraw::DrawViewDimension] Dimension003
  AngleOverride = false
  Arbitrary = false
  ArbitraryTolerances = false
  EqualTolerance = true
  ExtensionAngle = 0
  FormatSpec = %.2w
  FormatSpecOverTolerance = %+.2w
  FormatSpecUnderTolerance = %+.2w
  Inverted = false
  LineAngle = 0
  LockPosition = false
  MeasureType = 1
  OverTolerance = 0
  References2D = -> [View003]
  Rotation = 0
  ScaleType = 0
  TheoreticalExact = false
  Type = 1
  UnderTolerance = 0
  X = -0.439495
  Y = 76.0004
FEATURE [TechDraw::DrawViewDimension] Dimension004
  AngleOverride = false
  Arbitrary = false
  ArbitraryTolerances = false
  EqualTolerance = true
  ExtensionAngle = 0
  FormatSpec = %.2w
  FormatSpecOverTolerance = %+.2w
  FormatSpecUnderTolerance = %+.2w
  Inverted = false
  LineAngle = 0
  LockPosition = false
  MeasureType = 1
  OverTolerance = 0
  References2D = -> [View003]
  Rotation = 0
  ScaleType = 0
  TheoreticalExact = false
  Type = 1
  UnderTolerance = 0
  X = -0.219748
  Y = 82.6054
FEATURE [TechDraw::DrawViewDimension] Dimension005
  AngleOverride = false
  Arbitrary = false
  ArbitraryTolerances = false
  EqualTolerance = true
  ExtensionAngle = 0
  FormatSpec = %.2w
  FormatSpecOverTolerance = %+.2w
  FormatSpecUnderTolerance = %+.2w
  Inverted = false
  LineAngle = 0
  LockPosition = false
  MeasureType = 1
  OverTolerance = 0
  References2D = -> [View001]
  Rotation = 0
  ScaleType = 0
  TheoreticalExact = false
  Type = 1
  UnderTolerance = 0
  X = -9.47197
  Y = 76.7367
FEATURE [TechDraw::DrawViewDimension] Dimension006
  AngleOverride = false
  Arbitrary = false
  ArbitraryTolerances = false
  EqualTolerance = true
  ExtensionAngle = 0
  FormatSpec = %.2w
  FormatSpecOverTolerance = %+.2w
  FormatSpecUnderTolerance = %+.2w
  Inverted = false
  LineAngle = 0
  LockPosition = false
  MeasureType = 1
  OverTolerance = 0
  References2D = -> [View001]
  Rotation = 0
  ScaleType = 0
  TheoreticalExact = false
  Type = 1
  UnderTolerance = 0
  X = 2.02803
  Y = 76.7367
FEATURE [TechDraw::DrawViewDimension] Dimension007
  AngleOverride = false
  Arbitrary = false
  ArbitraryTolerances = false
  EqualTolerance = true
  ExtensionAngle = 0
  FormatSpec = %.2w
  FormatSpecOverTolerance = %+.2w
  FormatSpecUnderTolerance = %+.2w
  Inverted = false
  LineAngle = 0
  LockPosition = false
  MeasureType = 1
  OverTolerance = 0
  References2D = -> [View001]
  Rotation = 0
  ScaleType = 0
  TheoreticalExact = false
  Type = 1
  UnderTolerance = 0
  X = 1.61241
  Y = 62.069
FEATURE [TechDraw::DrawViewDimension] Dimension008
  AngleOverride = false
  Arbitrary = false
  ArbitraryTolerances = false
  EqualTolerance = true
  ExtensionAngle = 0
  FormatSpec = %.2w
  FormatSpecOverTolerance = %+.2w
  FormatSpecUnderTolerance = %+.2w
  Inverted = false
  LineAngle = 0
  LockPosition = false
  MeasureType = 1
  OverTolerance = 0
  References2D = -> [View001]
  Rotation = 0
  ScaleType = 0
  TheoreticalExact = false
  Type = 1
  UnderTolerance = 0
  X = -5.20415
  Y = -71.3897
FEATURE [TechDraw::DrawViewDimension] Dimension009
  AngleOverride = false
  Arbitrary = false
  ArbitraryTolerances = false
  EqualTolerance = true
  ExtensionAngle = 0
  FormatSpec = %.2w
  FormatSpecOverTolerance = %+.2w
  FormatSpecUnderTolerance = %+.2w
  Inverted = false
  LineAngle = 0
  LockPosition = false
  MeasureType = 1
  OverTolerance = 0
  References2D = -> [View001]
  Rotation = 0
  ScaleType = 0
  TheoreticalExact = false
  Type = 1
  UnderTolerance = 0
  X = 9.14693
  Y = -71.8062
FEATURE [TechDraw::DrawViewDimension] Dimension010
  AngleOverride = false
  Arbitrary = false
  ArbitraryTolerances = false
  EqualTolerance = true
  ExtensionAngle = 0
  FormatSpec = ⌀%.2w
  FormatSpecOverTolerance = %+.2w
  FormatSpecUnderTolerance = %+.2w
  Inverted = false
  LineAngle = 0
  LockPosition = false
  MeasureType = 1
  OverTolerance = 0
  References2D = -> [View003]
  Rotation = 0
  ScaleType = 0
  TheoreticalExact = false
  Type = 5
  UnderTolerance = 0
  X = -18
  Y = -44.5
FEATURE [TechDraw::DrawViewDimension] Dimension011
  AngleOverride = false
  Arbitrary = false
  ArbitraryTolerances = false
  EqualTolerance = true
  ExtensionAngle = 0
  FormatSpec = %.2w
  FormatSpecOverTolerance = %+.2w
  FormatSpecUnderTolerance = %+.2w
  Inverted = false
  LineAngle = 0
  LockPosition = false
  MeasureType = 1
  OverTolerance = 0
  References2D = -> [View001]
  Rotation = 0
  ScaleType = 0
  TheoreticalExact = false
  Type = 2
  UnderTolerance = 0
  X = -21.2934
  Y = 1.92227
FEATURE [TechDraw::DrawViewDimension] Dimension012
  AngleOverride = false
  Arbitrary = false
  ArbitraryTolerances = false
  EqualTolerance = true
  ExtensionAngle = 0
  FormatSpec = %.2w
  FormatSpecOverTolerance = %+.2w
  FormatSpecUnderTolerance = %+.2w
  Inverted = false
  LineAngle = 0
  LockPosition = false
  MeasureType = 1
  OverTolerance = 0
  References2D = -> [View]
  Rotation = 0
  ScaleType = 0
  TheoreticalExact = false
  Type = 1
  UnderTolerance = 0
  X = -1.50271
  Y = 75.0241
FEATURE [TechDraw::DrawViewDimension] Dimension013
  AngleOverride = false
  Arbitrary = false
  ArbitraryTolerances = false
  EqualTolerance = true
  ExtensionAngle = 0
  FormatSpec = %.2w
  FormatSpecOverTolerance = %+.2w
  FormatSpecUnderTolerance = %+.2w
  Inverted = false
  LineAngle = 0
  LockPosition = false
  MeasureType = 1
  OverTolerance = 0
  References2D = -> [View]
  Rotation = 0
  ScaleType = 0
  TheoreticalExact = false
  Type = 2
  UnderTolerance = 0
  X = -69.3074
  Y = 2.5
FEATURE [TechDraw::DrawViewDimension] Dimension014
  AngleOverride = false
  Arbitrary = false
  ArbitraryTolerances = false
  EqualTolerance = true
  ExtensionAngle = 0
  FormatSpec = %.2w
  FormatSpecOverTolerance = %+.2w
  FormatSpecUnderTolerance = %+.2w
  Inverted = false
  LineAngle = 0
  LockPosition = false
  MeasureType = 1
  OverTolerance = 0
  References2D = -> [View]
  Rotation = 0
  ScaleType = 0
  TheoreticalExact = false
  Type = 2
  UnderTolerance = 0
  X = -62.3074
  Y = 2.5
FEATURE [TechDraw::DrawViewDimension] Dimension015
  AngleOverride = false
  Arbitrary = false
  ArbitraryTolerances = false
  EqualTolerance = true
  ExtensionAngle = 0
  FormatSpec = R%.2w
  FormatSpecOverTolerance = %+.2w
  FormatSpecUnderTolerance = %+.2w
  Inverted = false
  LineAngle = 0
  LockPosition = false
  MeasureType = 1
  OverTolerance = 0
  References2D = -> [View]
  Rotation = 0
  ScaleType = 0
  TheoreticalExact = false
  Type = 4
  UnderTolerance = 0
  X = 50
  Y = -55
FEATURE [TechDraw::DrawViewDimension] Dimension020
  AngleOverride = false
  Arbitrary = false
  ArbitraryTolerances = false
  EqualTolerance = true
  ExtensionAngle = 0
  FormatSpec = %.2w
  FormatSpecOverTolerance = %+.2w
  FormatSpecUnderTolerance = %+.2w
  Inverted = false
  LineAngle = 0
  LockPosition = false
  MeasureType = 1
  OverTolerance = 0
  References2D = -> [View]
  Rotation = 0
  ScaleType = 0
  TheoreticalExact = false
  Type = 2
  UnderTolerance = 0
  X = -53.4614
  Y = 58.5
FEATURE [TechDraw::DrawViewDimension] Dimension021
  AngleOverride = false
  Arbitrary = false
  ArbitraryTolerances = false
  EqualTolerance = true
  ExtensionAngle = 0
  FormatSpec = %.2w
  FormatSpecOverTolerance = %+.2w
  FormatSpecUnderTolerance = %+.2w
  Inverted = false
  LineAngle = 0
  LockPosition = false
  MeasureType = 1
  OverTolerance = 0
  References2D = -> [View]
  Rotation = 0
  ScaleType = 0
  TheoreticalExact = false
  Type = 2
  UnderTolerance = 0
  X = -53.4614
  Y = -53.5
FEATURE [TechDraw::DrawViewDimension] Dimension022
  AngleOverride = false
  Arbitrary = false
  ArbitraryTolerances = false
  EqualTolerance = true
  ExtensionAngle = 0
  FormatSpec = %.2w
  FormatSpecOverTolerance = %+.2w
  FormatSpecUnderTolerance = %+.2w
  Inverted = false
  LineAngle = 0
  LockPosition = false
  MeasureType = 1
  OverTolerance = 0
  References2D = -> [View002]
  Rotation = 0
  ScaleType = 0
  TheoreticalExact = false
  Type = 1
  UnderTolerance = 0
  X = -5.97119
  Y = 82.1958
FEATURE [TechDraw::DrawViewDimension] Dimension023
  AngleOverride = false
  Arbitrary = false
  ArbitraryTolerances = false
  EqualTolerance = true
  ExtensionAngle = 0
  FormatSpec = %.2w
  FormatSpecOverTolerance = %+.2w
  FormatSpecUnderTolerance = %+.2w
  Inverted = false
  LineAngle = 0
  LockPosition = false
  MeasureType = 1
  OverTolerance = 0
  References2D = -> [View002]
  Rotation = 0
  ScaleType = 0
  TheoreticalExact = false
  Type = 1
  UnderTolerance = 0
  X = 0.028805
  Y = 82.1958
FEATURE [TechDraw::DrawViewDimension] Dimension024
  AngleOverride = false
  Arbitrary = false
  ArbitraryTolerances = false
  EqualTolerance = true
  ExtensionAngle = 0
  FormatSpec = %.2w
  FormatSpecOverTolerance = %+.2w
  FormatSpecUnderTolerance = %+.2w
  Inverted = false
  LineAngle = 0
  LockPosition = false
  MeasureType = 1
  OverTolerance = 0
  References2D = -> [View002]
  Rotation = 0
  ScaleType = 0
  TheoreticalExact = false
  Type = 1
  UnderTolerance = 0
  X = 6.02881
  Y = 82.1958
FEATURE [TechDraw::DrawViewDimension] Dimension025
  AngleOverride = false
  Arbitrary = false
  ArbitraryTolerances = false
  EqualTolerance = true
  ExtensionAngle = 0
  FormatSpec = %.2w
  FormatSpecOverTolerance = %+.2w
  FormatSpecUnderTolerance = %+.2w
  Inverted = false
  LineAngle = 0
  LockPosition = false
  MeasureType = 1
  OverTolerance = 0
  References2D = -> [View]
  Rotation = 0
  ScaleType = 0
  TheoreticalExact = false
  Type = 2
  UnderTolerance = 0
  X = -53.4614
  Y = 26.5
FEATURE [TechDraw::DrawViewDimension] Dimension026
  AngleOverride = false
  Arbitrary = false
  ArbitraryTolerances = false
  EqualTolerance = true
  ExtensionAngle = 0
  FormatSpec = %.2w
  FormatSpecOverTolerance = %+.2w
  FormatSpecUnderTolerance = %+.2w
  Inverted = false
  LineAngle = 0
  LockPosition = false
  MeasureType = 1
  OverTolerance = 0
  References2D = -> [View]
  Rotation = 0
  ScaleType = 0
  TheoreticalExact = false
  Type = 2
  UnderTolerance = 0
  X = -53.4614
  Y = -23.5
FEATURE [Sketcher::SketchObject] Sketch030  label="KeyholeInsertShape"
  FullyConstrained = true
  Placement = pos=(0,0,0) rot=(1,0,0;1.5708rad)
  sketch-geometry (8):
    g0: ArcOfCircle CenterX=1e-16 CenterY=0 CenterZ=0 NormalX=0 NormalY=0 NormalZ=1 AngleXU=0 Radius=2.75 StartAngle=5.28932 EndAngle=10.4186
    g1: LineSegment StartX=-1.5 StartY=-2.30489 StartZ=0 EndX=-1.5 EndY=-8 EndZ=0
    g2: LineSegment StartX=-1.5 StartY=-8 StartZ=0 EndX=1.5 EndY=-8 EndZ=0
    g3: LineSegment StartX=1.5 StartY=-8 StartZ=0 EndX=1.5 EndY=-2.30489 EndZ=0
    g4: ArcOfCircle CenterX=0 CenterY=3 CenterZ=0 NormalX=0 NormalY=0 NormalZ=1 AngleXU=0 Radius=7 StartAngle=2.6357e-12 EndAngle=3.14159
    g5: ArcOfCircle CenterX=0 CenterY=-8 CenterZ=0 NormalX=0 NormalY=0 NormalZ=1 AngleXU=0 Radius=7 StartAngle=3.14159 EndAngle=6.28319
    g6: LineSegment StartX=-7 StartY=3 StartZ=0 EndX=-7 EndY=-8 EndZ=0
    g7: LineSegment StartX=7 StartY=-8 StartZ=0 EndX=7 EndY=3 EndZ=0
  constraints (22):
    c: Coincident(g1,g0)
    c: Vertical(g1)
    c: Coincident(g2,g1)
    c: Horizontal(g2)
    c: Coincident(g3,g2)
    c: Coincident(g3,g0)
    c: Vertical(g3)
    c: Symmetric(g0,g0,g-2)
    c: Diameter(g0) = 5.5
    c: Distance(g2) = 3
    c: DistanceY(g2,g0) = 8
    c: Tangent(g4,g6) = -1.5708
    c: Tangent(g6,g5) = -1.5708
    c: Tangent(g5,g7) = -1.5708
    c: Tangent(g7,g4) = -1.5708
    c: Equal(g4,g5)
    c: PointOnObject(g5,g-2)
    c: Diameter(g4) = 14
    c: Coincident(g0,g-1)
    c: PointOnObject(g5,g2)
    c: DistanceY(g0,g4) = 3
    c: Vertical(g5,g4)
FEATURE [Part::Extrusion] Extrude024  label="KeyholeInsert"
  Base = -> Sketch030
  Dir = (0,-1,2e-16)
  DirMode = 2
  FaceMakerClass = Part::FaceMakerBullseye
  LengthFwd = 2
  LengthRev = 0
  Placement = pos=(0,-15,0) rot=(0,0,1;0rad)
  Solid = true
  Symmetric = false
FEATURE [App::DocumentObjectGroup] Group002  label="Lock"
  Group = -> [Extrude012,Extrude014,Sketch019,Sketch021,Extrude015,Extrude016,Extrude017,Fusion]
FEATURE [App::DocumentObjectGroup] Group003  label="LatchPlate"
  Group = -> [Extrude022,Extrude023]
FEATURE [Part::Cylinder] Cylinder  label="Shaft"
  Angle = 360
  AttacherType = Attacher::AttachEngine3D
  FirstAngle = 0
  Height = 30
  Placement = pos=(0,0,0) rot=(1,0,0;1.5708rad)
  Radius = 2.25
  SecondAngle = 0
FEATURE [Part::Cylinder] Cylinder001  label="Bow"
  Angle = 360
  AttacherType = Attacher::AttachEngine3D
  FirstAngle = 0
  Height = 2
  Placement = pos=(-1,-35,0) rot=(0,1,0;1.5708rad)
  Radius = 8
  SecondAngle = 0
FEATURE [Part::Box] Box  label="Bit"
  AttacherType = Attacher::AttachEngine3D
  Height = 8.75
  Length = 2
  Placement = pos=(-1,-6,-7.75) rot=(0,0,1;0rad)
  Width = 6
FEATURE [Part::MultiFuse] Fusion001  label="Key"
  Refine = true
  Shapes = -> [Cylinder,Cylinder001,Box]
FEATURE [TechDraw::DrawViewDimension] Dimension027
  AngleOverride = false
  Arbitrary = false
  ArbitraryTolerances = false
  EqualTolerance = true
  ExtensionAngle = 0
  FormatSpec = %.2w
  FormatSpecOverTolerance = %+.2w
  FormatSpecUnderTolerance = %+.2w
  Inverted = false
  LineAngle = 0
  LockPosition = false
  MeasureType = 1
  OverTolerance = 0
  References2D = -> [View]
  Rotation = 0
  ScaleType = 0
  TheoreticalExact = false
  Type = 2
  UnderTolerance = 0
  X = 59.7257
  Y = 3.81848
FEATURE [TechDraw::DrawViewDimension] Dimension029
  AngleOverride = false
  Arbitrary = false
  ArbitraryTolerances = false
  EqualTolerance = true
  ExtensionAngle = 0
  FormatSpec = %.2w
  FormatSpecOverTolerance = %+.2w
  FormatSpecUnderTolerance = %+.2w
  Inverted = false
  LineAngle = 0
  LockPosition = false
  MeasureType = 1
  OverTolerance = 0
  References2D = -> [View]
  Rotation = 0
  ScaleType = 0
  TheoreticalExact = false
  Type = 1
  UnderTolerance = 0
  X = -6.03773
  Y = -67
FEATURE [TechDraw::DrawViewDimension] Dimension030
  AngleOverride = false
  Arbitrary = false
  ArbitraryTolerances = false
  EqualTolerance = true
  ExtensionAngle = 0
  FormatSpec = %.2w
  FormatSpecOverTolerance = %+.2w
  FormatSpecUnderTolerance = %+.2w
  Inverted = false
  LineAngle = 0
  LockPosition = false
  MeasureType = 1
  OverTolerance = 0
  References2D = -> [View]
  Rotation = 0
  ScaleType = 0
  TheoreticalExact = false
  Type = 1
  UnderTolerance = 0
  X = 32.9623
  Y = -67
FEATURE [TechDraw::DrawViewDimension] Dimension031
  AngleOverride = false
  Arbitrary = false
  ArbitraryTolerances = false
  EqualTolerance = true
  ExtensionAngle = 0
  FormatSpec = %.2w
  FormatSpecOverTolerance = %+.2w
  FormatSpecUnderTolerance = %+.2w
  Inverted = false
  LineAngle = 0
  LockPosition = false
  MeasureType = 1
  OverTolerance = 0
  References2D = -> [View]
  Rotation = 0
  ScaleType = 0
  TheoreticalExact = false
  Type = 1
  UnderTolerance = 0
  X = -39.4793
  Y = -67
FEATURE [TechDraw::DrawPage] Page  label="LockAndLatchPlate"
  KeepUpdated = true
  NextBalloonIndex = 1
  ProjectionType = 0
  Template = -> Template
  Views = -> [View,View001,View002,View003,Dimension,Dimension001,Dimension002,Dimension003,Dimension004,Dimension005,Dimension006,Dimension007,Dimension008,Dimension009,Dimension010,Dimension011,Dimension012,Dimension013,Dimension014,Dimension015,Dimension020,Dimension021,Dimension022,Dimension023,Dimension024,Dimension025,Dimension026,Dimension027,Dimension029,Dimension030,Dimension031]
FEATURE [TechDraw::DrawHatch] Hatch  label="HatchF5"
  HatchPattern = <path>
  Source = -> View [Face5]
FEATURE [TechDraw::DrawHatch] Hatch001  label="Hatch001F13"
  HatchPattern = <path>
  Source = -> View [Face13]
FEATURE [TechDraw::DrawSVGTemplate] Template001
  EditableTexts = AUTHOR_NAME=Lukas Goßmann; DRAWING_TITLE=Schlüssel und Schlüsselschild; FC-DATE=10.06.2023; FC-REV=REV A; FC-SC=2:1; FC-SH=8/8; FC-SI=A3; SI-1=Schlüssel besteht aus Messing, Einzelteile verlötet; SI-2=Schlüssel und Schlüsselschild vergoldet
  Height = 297
  Orientation = 1
  Width = 420
FEATURE [TechDraw::DrawViewPart] View004
  CoarseView = false
  Direction = (1,0,0)
  Focus = 100
  HardHidden = false
  IsoCount = 0
  IsoHidden = false
  IsoVisible = false
  LockPosition = true
  Perspective = false
  Rotation = 0
  Scale = 2
  ScaleType = 2
  ScrubCount = 0
  SeamHidden = false
  SeamVisible = true
  SmoothHidden = false
  SmoothVisible = true
  Source = -> [Fusion001]
  X = 110.106
  XDirection = (0,1,0)
  Y = 200
FEATURE [TechDraw::DrawViewPart] View005
  CoarseView = false
  Direction = (0,-1,0)
  Focus = 100
  HardHidden = false
  IsoCount = 0
  IsoHidden = false
  IsoVisible = false
  LockPosition = true
  Perspective = false
  Rotation = 0
  Scale = 2
  ScaleType = 2
  ScrubCount = 0
  SeamHidden = false
  SeamVisible = true
  SmoothHidden = false
  SmoothVisible = true
  Source = -> [Extrude024]
  X = 299
  XDirection = (1,0,0)
  Y = 195
FEATURE [TechDraw::DrawViewDimension] Dimension032
  AngleOverride = false
  Arbitrary = false
  ArbitraryTolerances = false
  EqualTolerance = true
  ExtensionAngle = 0
  FormatSpec = ⌀%.2w
  FormatSpecOverTolerance = %+.2w
  FormatSpecUnderTolerance = %+.2w
  Inverted = false
  LineAngle = 0
  LockPosition = false
  MeasureType = 1
  OverTolerance = 0
  References2D = -> [View004]
  Rotation = 0
  ScaleType = 0
  TheoreticalExact = false
  Type = 5
  UnderTolerance = 0
  X = -53.7942
  Y = -18.1951
FEATURE [TechDraw::DrawViewDimension] Dimension033
  AngleOverride = false
  Arbitrary = false
  ArbitraryTolerances = false
  EqualTolerance = true
  ExtensionAngle = 0
  FormatSpec = %.2w
  FormatSpecOverTolerance = %+.2w
  FormatSpecUnderTolerance = %+.2w
  Inverted = false
  LineAngle = 0
  LockPosition = false
  MeasureType = 1
  OverTolerance = 0
  References2D = -> [View004]
  Rotation = 0
  ScaleType = 0
  TheoreticalExact = false
  Type = 2
  UnderTolerance = 0
  X = 50.2779
  Y = 2.5018
FEATURE [TechDraw::DrawViewDimension] Dimension035
  AngleOverride = false
  Arbitrary = false
  ArbitraryTolerances = false
  EqualTolerance = true
  ExtensionAngle = 0
  FormatSpec = %.2w
  FormatSpecOverTolerance = %+.2w
  FormatSpecUnderTolerance = %+.2w
  Inverted = false
  LineAngle = 0
  LockPosition = false
  MeasureType = 1
  OverTolerance = 0
  References2D = -> [View004]
  Rotation = 0
  ScaleType = 0
  TheoreticalExact = false
  Type = 1
  UnderTolerance = 0
  X = 37.0321
  Y = -17.6346
FEATURE [TechDraw::DrawViewDimension] Dimension036
  AngleOverride = false
  Arbitrary = false
  ArbitraryTolerances = false
  EqualTolerance = true
  ExtensionAngle = 0
  FormatSpec = %.2w
  FormatSpecOverTolerance = %+.2w
  FormatSpecUnderTolerance = %+.2w
  Inverted = false
  LineAngle = 0
  LockPosition = false
  MeasureType = 1
  OverTolerance = 0
  References2D = -> [View004]
  Rotation = 0
  ScaleType = 0
  TheoreticalExact = false
  Type = 1
  UnderTolerance = 0
  X = 8.03208
  Y = 31.9683
FEATURE [TechDraw::DrawViewDimension] Dimension038
  AngleOverride = false
  Arbitrary = false
  ArbitraryTolerances = false
  EqualTolerance = true
  ExtensionAngle = 0
  FormatSpec = %.2w
  FormatSpecOverTolerance = %+.2w
  FormatSpecUnderTolerance = %+.2w
  Inverted = false
  LineAngle = 0
  LockPosition = false
  MeasureType = 1
  OverTolerance = 0
  References2D = -> [View004]
  Rotation = 0
  ScaleType = 0
  TheoreticalExact = false
  Type = 1
  UnderTolerance = 0
  X = 13.0321
  Y = 24.9683
FEATURE [TechDraw::DrawViewDimension] Dimension039
  AngleOverride = false
  Arbitrary = false
  ArbitraryTolerances = false
  EqualTolerance = true
  ExtensionAngle = 0
  FormatSpec = ⌀%.2w
  FormatSpecOverTolerance = %+.2w
  FormatSpecUnderTolerance = %+.2w
  Inverted = false
  LineAngle = 0
  LockPosition = false
  MeasureType = 1
  OverTolerance = 0
  References2D = -> [View005]
  Rotation = 0
  ScaleType = 0
  TheoreticalExact = false
  Type = 5
  UnderTolerance = 0
  X = 18.3635
  Y = 25.5295
FEATURE [TechDraw::DrawViewDimension] Dimension040
  AngleOverride = false
  Arbitrary = false
  ArbitraryTolerances = false
  EqualTolerance = true
  ExtensionAngle = 0
  FormatSpec = %.2w
  FormatSpecOverTolerance = %+.2w
  FormatSpecUnderTolerance = %+.2w
  Inverted = false
  LineAngle = 0
  LockPosition = false
  MeasureType = 1
  OverTolerance = 0
  References2D = -> [View005]
  Rotation = 0
  ScaleType = 0
  TheoreticalExact = false
  Type = 1
  UnderTolerance = 0
  X = 0
  Y = -34.8481
FEATURE [TechDraw::DrawViewDimension] Dimension041
  AngleOverride = false
  Arbitrary = false
  ArbitraryTolerances = false
  EqualTolerance = true
  ExtensionAngle = 0
  FormatSpec = %.2w
  FormatSpecOverTolerance = %+.2w
  FormatSpecUnderTolerance = %+.2w
  Inverted = false
  LineAngle = 0
  LockPosition = false
  MeasureType = 1
  OverTolerance = 0
  References2D = -> [View005]
  Rotation = 0
  ScaleType = 0
  TheoreticalExact = false
  Type = 2
  UnderTolerance = 0
  X = -22.4745
  Y = 1.91956
FEATURE [TechDraw::DrawViewDimension] Dimension042
  AngleOverride = false
  Arbitrary = false
  ArbitraryTolerances = false
  EqualTolerance = true
  ExtensionAngle = 0
  FormatSpec = %.2w
  FormatSpecOverTolerance = %+.2w
  FormatSpecUnderTolerance = %+.2w
  Inverted = false
  LineAngle = 0
  LockPosition = false
  MeasureType = 1
  OverTolerance = 0
  References2D = -> [View005]
  Rotation = 0
  ScaleType = 0
  TheoreticalExact = false
  Type = 1
  UnderTolerance = 0
  X = 0
  Y = -27.8481
FEATURE [TechDraw::DrawViewDimension] Dimension043
  AngleOverride = false
  Arbitrary = false
  ArbitraryTolerances = false
  EqualTolerance = true
  ExtensionAngle = 0
  FormatSpec = %.2w
  FormatSpecOverTolerance = %+.2w
  FormatSpecUnderTolerance = %+.2w
  Inverted = false
  LineAngle = 0
  LockPosition = false
  MeasureType = 1
  OverTolerance = 0
  References2D = -> [View005]
  Rotation = 0
  ScaleType = 0
  TheoreticalExact = false
  Type = 2
  UnderTolerance = 0
  X = 21.5248
  Y = -0.822468
FEATURE [TechDraw::DrawViewDimension] Dimension037
  AngleOverride = false
  Arbitrary = false
  ArbitraryTolerances = false
  EqualTolerance = true
  ExtensionAngle = 0
  FormatSpec = %.2w
  FormatSpecOverTolerance = %+.2w
  FormatSpecUnderTolerance = %+.2w
  Inverted = false
  LineAngle = 0
  LockPosition = false
  MeasureType = 1
  OverTolerance = 0
  References2D = -> [View004]
  Rotation = 0
  ScaleType = 0
  TheoreticalExact = false
  Type = 2
  UnderTolerance = 0
  X = 50.2779
  Y = -7.4982
FEATURE [TechDraw::DrawViewDimension] Dimension044
  AngleOverride = false
  Arbitrary = false
  ArbitraryTolerances = false
  EqualTolerance = true
  ExtensionAngle = 0
  FormatSpec = %.2w
  FormatSpecOverTolerance = %+.2w
  FormatSpecUnderTolerance = %+.2w
  Inverted = false
  LineAngle = 0
  LockPosition = false
  MeasureType = 1
  OverTolerance = 0
  References2D = -> [View004]
  Rotation = 0
  ScaleType = 0
  TheoreticalExact = false
  Type = 2
  UnderTolerance = 0
  X = 50.2779
  Y = -7.4982
FEATURE [TechDraw::DrawPage] Page001  label="KeyAndKeyholeInsert"
  KeepUpdated = true
  NextBalloonIndex = 1
  ProjectionType = 0
  Template = -> Template001
  Views = -> [View004,View005,Dimension032,Dimension033,Dimension035,Dimension036,Dimension037,Dimension038,Dimension039,Dimension040,Dimension041,Dimension042,Dimension043,Dimension044]
FEATURE [TechDraw::DrawHatch] Hatch002  label="Hatch002F2"
  HatchPattern = <path>
  Source = -> View [Face2]
note: 3 file-system paths scrubbed to <path> (originals preserved in the JSON sidecar)
